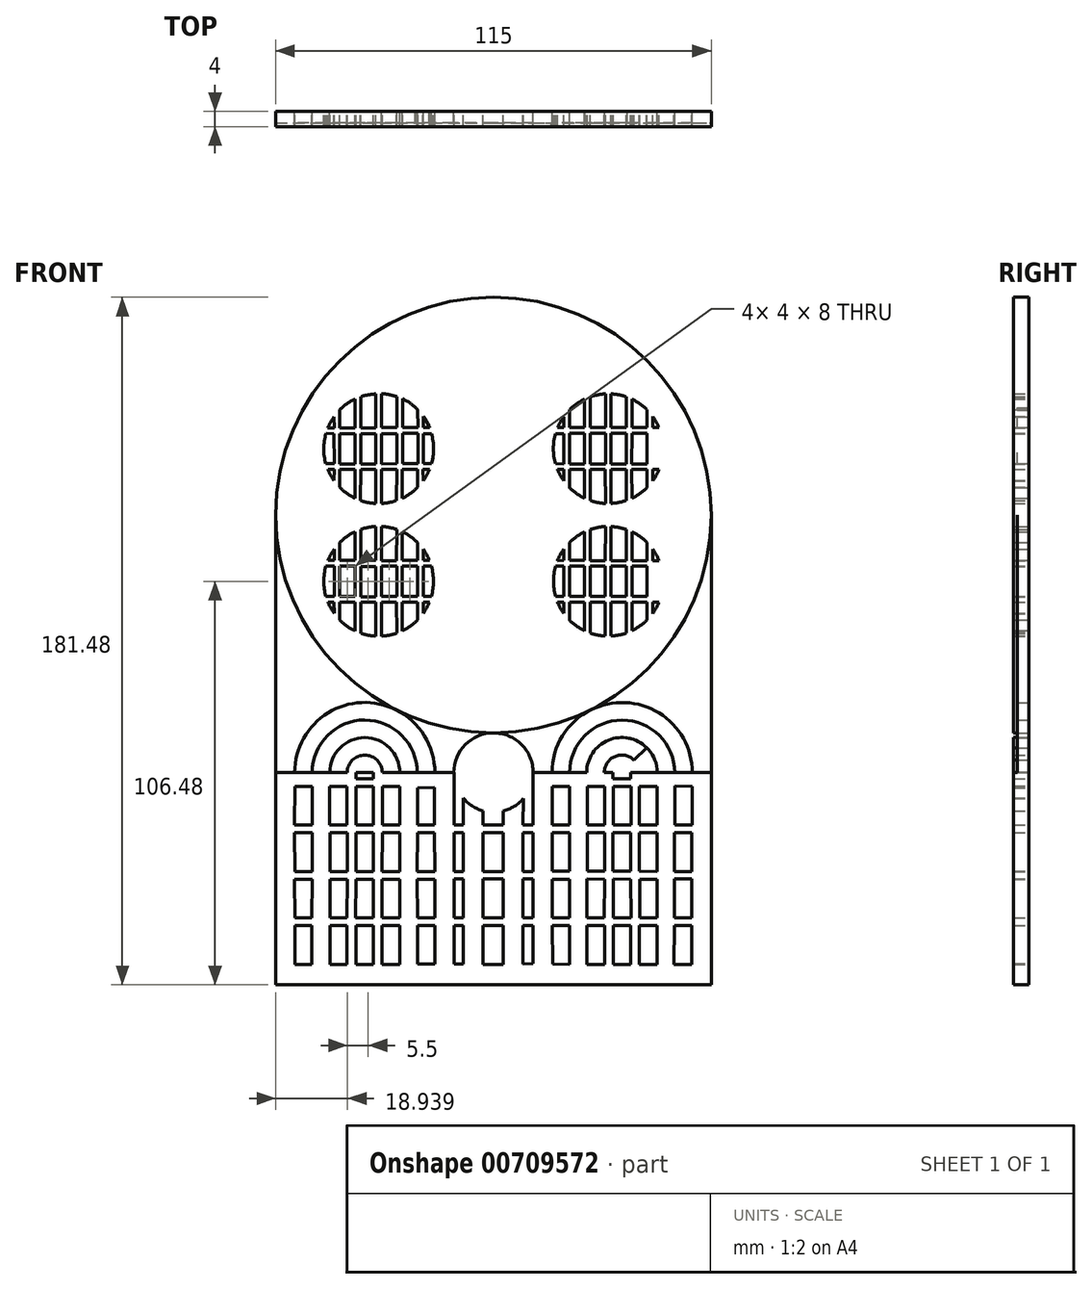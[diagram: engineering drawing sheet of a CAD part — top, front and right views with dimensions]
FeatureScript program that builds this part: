
annotation { "Feature Type Name" : "Feature", "Feature Type Description" : "" }
export const myFeature = defineFeature(function(context is Context, id is Id, definition is map)
    precondition{}
    {
        {
            var Q0;
            Q0=qCreatedBy(makeId("Front.planeOp"),FACE);
            var sketch = newSketch(context, id + "F0", { "sketchPlane" : qUnion([Q0])});
            skCircle(sketch, "E0", {"center": v(0, 0) * mm, "radius": 17.5 * mm});
            skPoint(sketch, "E1", {"position": v(0, 35) * mm});
            skPoint(sketch, "E2", {"position": v(-35, 0) * mm});
            skPoint(sketch, "E3", {"position": v(35, 0) * mm});
            skPoint(sketch, "E4", {"position": v(0, -35) * mm});
            skCircle(sketch, "E5", {"center": v(0, 0) * mm, "radius": 35 * mm});
            skPoint(sketch, "E6", {"position": v(-30.31, 17.5) * mm});
            skPoint(sketch, "E7", {"position": v(30.31, 17.5) * mm});
            skPoint(sketch, "E8", {"position": v(30.31, -17.5) * mm});
            skPoint(sketch, "E9", {"position": v(-30.31, -17.5) * mm});
            skCircle(sketch, "E10", {"center": v(-30.31, 17.5) * mm, "radius": 17.5 * mm});
            skCircle(sketch, "E11", {"center": v(30.31, 17.5) * mm, "radius": 17.5 * mm});
            skPoint(sketch, "E12", {"position": v(15.16, 8.75) * mm});
            skPoint(sketch, "E13", {"position": v(-15.16, -8.75) * mm});
            skCircle(sketch, "E14", {"center": v(-30.31, -17.5) * mm, "radius": 17.5 * mm});
            skCircle(sketch, "E15", {"center": v(0, -35) * mm, "radius": 17.5 * mm});
            skCircle(sketch, "E16", {"center": v(30.31, -17.5) * mm, "radius": 17.5 * mm});
            skCircle(sketch, "E17", {"center": v(0, 35) * mm, "radius": 17.5 * mm});
            skPoint(sketch, "E18", {"position": v(0, -52.5) * mm});
            skCircle(sketch, "E19", {"center": v(0, 0) * mm, "radius": 14.5 * mm});
            skCircle(sketch, "E20", {"center": v(-30.31, 17.5) * mm, "radius": 14.5 * mm});
            skCircle(sketch, "E21", {"center": v(0, 35) * mm, "radius": 14.5 * mm});
            skCircle(sketch, "E22", {"center": v(30.31, 17.5) * mm, "radius": 14.5 * mm});
            skCircle(sketch, "E23", {"center": v(30.31, -17.5) * mm, "radius": 14.5 * mm});
            skCircle(sketch, "E24", {"center": v(0, -35) * mm, "radius": 14.5 * mm});
            skCircle(sketch, "E25", {"center": v(-30.31, -17.5) * mm, "radius": 14.5 * mm});
            skArc(sketch, "E26", {"start": v(57.5, 0) * mm, "mid": v(0, 57.5) * mm, "end": v(-57.5, 0) * mm});
            skPoint(sketch, "E27", {"position": v(-20.96, 36.3) * mm});
            skArc(sketch, "E28", {"start": v(-20.96, 36.3) * mm, "mid": v(-28.74, 38.44) * mm, "end": v(-36.76, 37.49) * mm});
            skArc(sketch, "E29", {"start": v(-20.96, 36.3) * mm, "mid": v(-18.92, 44.11) * mm, "end": v(-14.09, 50.57) * mm});
            skPoint(sketch, "E30", {"position": v(14.09, 50.58) * mm});
            skPoint(sketch, "E31", {"position": v(41.92, 0) * mm});
            skArc(sketch, "E32", {"start": v(50.84, 13.09) * mm, "mid": v(47.66, 5.67) * mm, "end": v(41.92, 0) * mm});
            skArc(sketch, "E33", {"start": v(41.92, 0) * mm, "mid": v(47.66, -5.67) * mm, "end": v(50.84, -13.09) * mm});
            skPoint(sketch, "E34", {"position": v(20.96, 36.3) * mm});
            skArc(sketch, "E35", {"start": v(20.96, 36.3) * mm, "mid": v(28.74, 38.44) * mm, "end": v(36.76, 37.49) * mm});
            skArc(sketch, "E36", {"start": v(14.09, 50.58) * mm, "mid": v(18.92, 44.11) * mm, "end": v(20.96, 36.3) * mm});
            skArc(sketch, "E37", {"start": v(-50.84, -13.09) * mm, "mid": v(-47.66, -5.67) * mm, "end": v(-41.92, 0) * mm});
            skArc(sketch, "E38", {"start": v(-50.84, 13.09) * mm, "mid": v(-47.66, 5.67) * mm, "end": v(-41.92, 0) * mm});
            skArc(sketch, "E39", {"start": v(-50.84, -13.09) * mm, "mid": v(-52.5, 0) * mm, "end": v(-50.84, 13.09) * mm});
            skArc(sketch, "E40", {"start": v(-36.76, -37.49) * mm, "mid": v(-28.74, -38.44) * mm, "end": v(-20.96, -36.3) * mm});
            skArc(sketch, "E41", {"start": v(-20.96, -36.3) * mm, "mid": v(-18.92, -44.11) * mm, "end": v(-14.09, -50.58) * mm});
            skArc(sketch, "E42", {"start": v(-36.76, -37.49) * mm, "mid": v(-26.25, -45.47) * mm, "end": v(-14.09, -50.58) * mm});
            skArc(sketch, "E43", {"start": v(14.09, -50.58) * mm, "mid": v(18.92, -44.11) * mm, "end": v(20.96, -36.3) * mm});
            skArc(sketch, "E44", {"start": v(20.96, -36.3) * mm, "mid": v(28.74, -38.44) * mm, "end": v(36.76, -37.49) * mm});
            skArc(sketch, "E45", {"start": v(14.09, -50.58) * mm, "mid": v(26.25, -45.47) * mm, "end": v(36.76, -37.49) * mm});
            skArc(sketch, "E46", {"start": v(50.84, -13.09) * mm, "mid": v(52.5, 0) * mm, "end": v(50.84, 13.09) * mm, "construction": true});
            skArc(sketch, "E47", {"start": v(14.09, 50.58) * mm, "mid": v(26.25, 45.47) * mm, "end": v(36.76, 37.49) * mm});
            skArc(sketch, "E48", {"start": v(-36.76, 37.49) * mm, "mid": v(-26.25, 45.47) * mm, "end": v(-14.09, 50.58) * mm});
            skLineSegment(sketch, "E49", {"start": v(0, 0) * mm, "end": v(47.13, 81.64) * mm, "construction": true});
            skArc(sketch, "E50", {"start": v(50.84, 13.09) * mm, "mid": v(52.5, 0) * mm, "end": v(50.84, -13.09) * mm});
            skSolve(sketch);
        }
        {
            var Q0;
            Q0=qCreatedBy(makeId("Front.planeOp"),FACE);
            var sketch = newSketch(context, id + "F1", { "sketchPlane" : qUnion([Q0])});
            skArc(sketch, "E51", {"start": v(57.5, 0) * mm, "mid": v(0, 57.5) * mm, "end": v(-57.5, 0) * mm});
            skLineSegment(sketch, "E52", {"start": v(57.5, -67.99) * mm, "end": v(57.5, 0) * mm});
            skLineSegment(sketch, "E53", {"start": v(-57.5, 0) * mm, "end": v(-57.5, -67.99) * mm});
            skPoint(sketch, "E54", {"position": v(-52.5, -67.99) * mm});
            skLineSegment(sketch, "E55", {"start": v(-52.5, -67.99) * mm, "end": v(52.5, -67.99) * mm});
            skPoint(sketch, "E56", {"position": v(-52.5, -23.45) * mm});
            skLineSegment(sketch, "E57", {"start": v(-52.5, -23.45) * mm, "end": v(-52.5, -67.99) * mm});
            skLineSegment(sketch, "E58", {"start": v(52.5, -23.45) * mm, "end": v(52.5, -67.99) * mm});
            skArc(sketch, "E59", {"start": v(-52.5, -23.45) * mm, "mid": v(-31.29, -48.24) * mm, "end": v(0, -57.5) * mm});
            skArc(sketch, "E60", {"start": v(0, -57.5) * mm, "mid": v(31.29, -48.24) * mm, "end": v(52.5, -23.45) * mm});
            skArc(sketch, "E61", {"start": v(-15.48, -67.99) * mm, "mid": v(-33.99, -49.48) * mm, "end": v(-52.5, -67.99) * mm});
            skArc(sketch, "E62", {"start": v(52.5, -67.99) * mm, "mid": v(33.99, -49.48) * mm, "end": v(15.48, -67.99) * mm});
            skArc(sketch, "E63", {"start": v(-10.48, -67.99) * mm, "mid": v(0, -57.5) * mm, "end": v(10.48, -67.99) * mm});
            skLineSegment(sketch, "E64", {"start": v(-10.48, -67.99) * mm, "end": v(-10.48, -73.7) * mm, "construction": true});
            skLineSegment(sketch, "E65", {"start": v(10.48, -67.99) * mm, "end": v(10.48, -74.15) * mm, "construction": true});
            skLineSegment(sketch, "E66", {"start": v(15.48, -67.99) * mm, "end": v(15.48, -73.84) * mm, "construction": true});
            skLineSegment(sketch, "E67", {"start": v(52.5, -67.99) * mm, "end": v(52.5, -74.35) * mm, "construction": true});
            skLineSegment(sketch, "E68", {"start": v(-15.48, -67.99) * mm, "end": v(-15.48, -74.15) * mm, "construction": true});
            skLineSegment(sketch, "E69", {"start": v(-52.5, -67.99) * mm, "end": v(-52.5, -75.2) * mm, "construction": true});
            skLineSegment(sketch, "E70", {"start": v(-15.48, -72) * mm, "end": v(-10.48, -72) * mm, "construction": true});
            skLineSegment(sketch, "E71", {"start": v(10.48, -71.6) * mm, "end": v(15.49, -71.6) * mm, "construction": true});
            skLineSegment(sketch, "E72", {"start": v(52.5, -67.99) * mm, "end": v(57.5, -67.99) * mm, "construction": true});
            skLineSegment(sketch, "E73", {"start": v(-52.5, -67.99) * mm, "end": v(-57.5, -67.99) * mm, "construction": true});
            skCircle(sketch, "E74", {"center": v(0, 0) * mm, "radius": 57.5 * mm});
            skLineSegment(sketch, "E75", {"start": v(15.49, -71.6) * mm, "end": v(20.11, -71.6) * mm, "construction": true});
            skLineSegment(sketch, "E76", {"start": v(20.11, -71.6) * mm, "end": v(24.74, -71.6) * mm, "construction": true});
            skLineSegment(sketch, "E77", {"start": v(24.74, -71.6) * mm, "end": v(29.36, -71.6) * mm, "construction": true});
            skLineSegment(sketch, "E78", {"start": v(29.36, -71.6) * mm, "end": v(33.99, -71.6) * mm, "construction": true});
            skLineSegment(sketch, "E79", {"start": v(33.99, -71.6) * mm, "end": v(38.62, -71.6) * mm, "construction": true});
            skLineSegment(sketch, "E80", {"start": v(38.62, -71.6) * mm, "end": v(43.24, -71.6) * mm, "construction": true});
            skLineSegment(sketch, "E81", {"start": v(43.24, -71.6) * mm, "end": v(47.87, -71.6) * mm, "construction": true});
            skLineSegment(sketch, "E82", {"start": v(47.87, -71.6) * mm, "end": v(52.5, -71.6) * mm, "construction": true});
            skLineSegment(sketch, "E83", {"start": v(20.11, -71.6) * mm, "end": v(20.11, -67.99) * mm, "construction": true});
            skLineSegment(sketch, "E84", {"start": v(24.74, -71.6) * mm, "end": v(24.74, -67.99) * mm, "construction": true});
            skLineSegment(sketch, "E85", {"start": v(29.36, -71.6) * mm, "end": v(29.36, -67.99) * mm, "construction": true});
            skLineSegment(sketch, "E86", {"start": v(33.99, -71.6) * mm, "end": v(33.99, -67.99) * mm, "construction": true});
            skLineSegment(sketch, "E87", {"start": v(38.62, -71.6) * mm, "end": v(38.62, -67.99) * mm, "construction": true});
            skLineSegment(sketch, "E88", {"start": v(43.24, -71.6) * mm, "end": v(43.24, -67.99) * mm, "construction": true});
            skLineSegment(sketch, "E89", {"start": v(47.87, -71.6) * mm, "end": v(47.87, -67.99) * mm, "construction": true});
            skArc(sketch, "E90", {"start": v(47.87, -67.99) * mm, "mid": v(33.99, -54.1) * mm, "end": v(20.11, -67.99) * mm});
            skArc(sketch, "E91", {"start": v(43.24, -67.99) * mm, "mid": v(33.99, -58.74) * mm, "end": v(24.74, -67.99) * mm});
            skArc(sketch, "E92", {"start": v(38.62, -67.99) * mm, "mid": v(33.99, -63.36) * mm, "end": v(29.36, -67.99) * mm});
            skLineSegment(sketch, "E93", {"start": v(-15.48, -72) * mm, "end": v(-20.11, -72) * mm, "construction": true});
            skLineSegment(sketch, "E94", {"start": v(-20.11, -72) * mm, "end": v(-24.74, -72) * mm, "construction": true});
            skLineSegment(sketch, "E95", {"start": v(-24.74, -72) * mm, "end": v(-29.36, -72) * mm, "construction": true});
            skLineSegment(sketch, "E96", {"start": v(-29.36, -72) * mm, "end": v(-33.99, -72) * mm, "construction": true});
            skLineSegment(sketch, "E97", {"start": v(-33.99, -72) * mm, "end": v(-38.62, -72) * mm, "construction": true});
            skLineSegment(sketch, "E98", {"start": v(-38.62, -72) * mm, "end": v(-43.24, -72) * mm, "construction": true});
            skLineSegment(sketch, "E99", {"start": v(-43.24, -72) * mm, "end": v(-47.87, -72) * mm, "construction": true});
            skLineSegment(sketch, "E100", {"start": v(-47.87, -72) * mm, "end": v(-52.5, -72) * mm, "construction": true});
            skLineSegment(sketch, "E101", {"start": v(-47.87, -72) * mm, "end": v(-47.87, -67.99) * mm, "construction": true});
            skLineSegment(sketch, "E102", {"start": v(-43.24, -72) * mm, "end": v(-43.24, -67.99) * mm, "construction": true});
            skLineSegment(sketch, "E103", {"start": v(-38.62, -72) * mm, "end": v(-38.62, -67.99) * mm, "construction": true});
            skLineSegment(sketch, "E104", {"start": v(-29.36, -72) * mm, "end": v(-29.36, -67.99) * mm, "construction": true});
            skLineSegment(sketch, "E105", {"start": v(-24.74, -72) * mm, "end": v(-24.74, -67.99) * mm, "construction": true});
            skLineSegment(sketch, "E106", {"start": v(-20.11, -72) * mm, "end": v(-20.11, -67.99) * mm, "construction": true});
            skLineSegment(sketch, "E107", {"start": v(-33.99, -72) * mm, "end": v(-33.99, -67.99) * mm, "construction": true});
            skArc(sketch, "E108", {"start": v(-20.11, -67.99) * mm, "mid": v(-33.99, -54.1) * mm, "end": v(-47.87, -67.99) * mm});
            skArc(sketch, "E109", {"start": v(-24.74, -67.99) * mm, "mid": v(-33.99, -58.74) * mm, "end": v(-43.24, -67.99) * mm});
            skArc(sketch, "E110", {"start": v(-29.36, -67.99) * mm, "mid": v(-33.99, -63.36) * mm, "end": v(-38.62, -67.99) * mm});
            skLineSegment(sketch, "E111", {"start": v(-10.48, -72) * mm, "end": v(-7.86, -72) * mm, "construction": true});
            skLineSegment(sketch, "E112", {"start": v(-7.86, -72) * mm, "end": v(-5.24, -72) * mm, "construction": true});
            skLineSegment(sketch, "E113", {"start": v(-5.24, -72) * mm, "end": v(-2.62, -72) * mm, "construction": true});
            skLineSegment(sketch, "E114", {"start": v(-2.62, -72) * mm, "end": v(0, -72) * mm, "construction": true});
            skLineSegment(sketch, "E115", {"start": v(0, -72) * mm, "end": v(2.62, -72) * mm, "construction": true});
            skLineSegment(sketch, "E116", {"start": v(2.62, -72) * mm, "end": v(5.24, -72) * mm, "construction": true});
            skLineSegment(sketch, "E117", {"start": v(5.24, -72) * mm, "end": v(7.86, -72) * mm, "construction": true});
            skLineSegment(sketch, "E118", {"start": v(7.86, -72) * mm, "end": v(10.48, -72) * mm, "construction": true});
            skLineSegment(sketch, "E119", {"start": v(-7.86, -72) * mm, "end": v(-7.86, -67.99) * mm, "construction": true});
            skLineSegment(sketch, "E120", {"start": v(-5.24, -72) * mm, "end": v(-5.24, -67.99) * mm, "construction": true});
            skLineSegment(sketch, "E121", {"start": v(-2.62, -72) * mm, "end": v(-2.62, -67.99) * mm, "construction": true});
            skLineSegment(sketch, "E122", {"start": v(2.62, -72) * mm, "end": v(2.62, -67.99) * mm, "construction": true});
            skLineSegment(sketch, "E123", {"start": v(0, -72) * mm, "end": v(0, -67.98) * mm, "construction": true});
            skLineSegment(sketch, "E124", {"start": v(5.24, -72) * mm, "end": v(5.24, -67.99) * mm, "construction": true});
            skLineSegment(sketch, "E125", {"start": v(7.86, -72) * mm, "end": v(7.86, -67.99) * mm, "construction": true});
            skArc(sketch, "E126", {"start": v(7.86, -67.99) * mm, "mid": v(0, -60.13) * mm, "end": v(-7.86, -67.99) * mm});
            skArc(sketch, "E127", {"start": v(5.24, -67.99) * mm, "mid": v(0, -62.75) * mm, "end": v(-5.24, -67.99) * mm});
            skArc(sketch, "E128", {"start": v(2.62, -67.99) * mm, "mid": v(0, -65.37) * mm, "end": v(-2.62, -67.99) * mm});
            skLineSegment(sketch, "E129", {"start": v(-33.99, -67.99) * mm, "end": v(-33.99, -49.48) * mm, "construction": true});
            skLineSegment(sketch, "E130", {"start": v(33.99, -67.99) * mm, "end": v(33.99, -49.48) * mm, "construction": true});
            skLineSegment(sketch, "E131", {"start": v(0, -57.5) * mm, "end": v(0, -67.98) * mm, "construction": true});
            skLineSegment(sketch, "E132", {"start": v(-33.99, -67.99) * mm, "end": v(-47.08, -54.9) * mm, "construction": true});
            skLineSegment(sketch, "E133", {"start": v(-33.99, -67.99) * mm, "end": v(-20.9, -54.9) * mm, "construction": true});
            skLineSegment(sketch, "E134", {"start": v(33.99, -67.99) * mm, "end": v(20.9, -54.9) * mm, "construction": true});
            skLineSegment(sketch, "E135", {"start": v(33.99, -67.99) * mm, "end": v(47.08, -54.9) * mm, "construction": true});
            skLineSegment(sketch, "E136", {"start": v(0, -67.98) * mm, "end": v(7.41, -60.57) * mm, "construction": true});
            skLineSegment(sketch, "E137", {"start": v(0, -67.98) * mm, "end": v(-7.41, -60.57) * mm, "construction": true});
            skLineSegment(sketch, "E138", {"start": v(-57.5, -67.99) * mm, "end": v(-52.5, -67.99) * mm});
            skLineSegment(sketch, "E139", {"start": v(52.5, -67.99) * mm, "end": v(57.5, -67.99) * mm});
            skPoint(sketch, "E140", {"position": v(-29.56, -3.02) * mm});
            skPoint(sketch, "E141", {"position": v(-42.06, -21.5) * mm});
            skLineSegment(sketch, "E142.bottom", {"start": v(-40.56, -13.5) * mm, "end": v(-40.56, -13.5) * mm});
            skLineSegment(sketch, "E142.top", {"start": v(-40.56, -21.5) * mm, "end": v(-40.56, -21.5) * mm});
            skLineSegment(sketch, "E142.left", {"start": v(-40.56, -13.5) * mm, "end": v(-40.56, -21.5) * mm});
            skLineSegment(sketch, "E142.right", {"start": v(-40.56, -13.5) * mm, "end": v(-40.56, -21.5) * mm});
            skLineSegment(sketch, "E143.bottom", {"start": v(-36.56, -21.5) * mm, "end": v(-36.57, -21.5) * mm});
            skLineSegment(sketch, "E143.top", {"start": v(-36.56, -13.5) * mm, "end": v(-36.57, -13.5) * mm});
            skLineSegment(sketch, "E143.left", {"start": v(-36.57, -21.5) * mm, "end": v(-36.57, -13.5) * mm});
            skLineSegment(sketch, "E143.right", {"start": v(-36.56, -21.5) * mm, "end": v(-36.56, -13.5) * mm});
            skLineSegment(sketch, "E144.bottom", {"start": v(-35.06, -13.56) * mm, "end": v(-31.06, -13.56) * mm});
            skLineSegment(sketch, "E144.top", {"start": v(-35.06, -21.56) * mm, "end": v(-31.06, -21.56) * mm});
            skLineSegment(sketch, "E144.left", {"start": v(-35.06, -13.56) * mm, "end": v(-35.06, -21.56) * mm});
            skLineSegment(sketch, "E144.right", {"start": v(-31.06, -13.56) * mm, "end": v(-31.06, -21.56) * mm});
            skLineSegment(sketch, "E145.bottom", {"start": v(-29.56, -13.52) * mm, "end": v(-25.56, -13.52) * mm});
            skLineSegment(sketch, "E145.top", {"start": v(-29.56, -21.52) * mm, "end": v(-25.56, -21.52) * mm});
            skLineSegment(sketch, "E145.left", {"start": v(-29.56, -13.52) * mm, "end": v(-29.56, -21.52) * mm});
            skLineSegment(sketch, "E145.right", {"start": v(-25.56, -13.52) * mm, "end": v(-25.56, -21.52) * mm});
            skLineSegment(sketch, "E146.bottom", {"start": v(-24.06, -13.5) * mm, "end": v(-20.06, -13.5) * mm});
            skLineSegment(sketch, "E146.top", {"start": v(-24.06, -21.5) * mm, "end": v(-20.06, -21.5) * mm});
            skLineSegment(sketch, "E146.left", {"start": v(-24.06, -13.5) * mm, "end": v(-24.06, -21.5) * mm});
            skLineSegment(sketch, "E146.right", {"start": v(-20.06, -13.5) * mm, "end": v(-20.06, -21.5) * mm});
            skLineSegment(sketch, "E147.bottom", {"start": v(-40.56, -13.5) * mm, "end": v(-36.57, -13.5) * mm});
            skLineSegment(sketch, "E147.top", {"start": v(-40.56, -21.5) * mm, "end": v(-36.57, -21.5) * mm});
            skLineSegment(sketch, "E147.right", {"start": v(-36.57, -13.5) * mm, "end": v(-36.57, -21.5) * mm});
            skLineSegment(sketch, "E148.bottom", {"start": v(-35.06, -23) * mm, "end": v(-31.06, -23) * mm});
            skLineSegment(sketch, "E149.bottom", {"start": v(-29.56, -23) * mm, "end": v(-25.57, -23) * mm});
            skLineSegment(sketch, "E150", {"start": v(-40.56, -13.5) * mm, "end": v(-36.56, -13.5) * mm});
            skLineSegment(sketch, "E151", {"start": v(-40.56, -12) * mm, "end": v(-36.56, -12) * mm});
            skLineSegment(sketch, "E152", {"start": v(-29.56, -12.02) * mm, "end": v(-25.56, -12.02) * mm});
            skLineSegment(sketch, "E153", {"start": v(-24.06, -12) * mm, "end": v(-20.06, -12) * mm});
            skLineSegment(sketch, "E154", {"start": v(-35.3, -3.87) * mm, "end": v(-35.3, -3.86) * mm});
            skLineSegment(sketch, "E155", {"start": v(-40.56, -23) * mm, "end": v(-36.56, -23) * mm});
            skLineSegment(sketch, "E156", {"start": v(-44.24, -13.5) * mm, "end": v(-42.06, -13.5) * mm});
            skLineSegment(sketch, "E157", {"start": v(-42.06, -13.5) * mm, "end": v(-42.06, -21.5) * mm});
            skLineSegment(sketch, "E158", {"start": v(-18.56, -21.5) * mm, "end": v(-16.38, -21.5) * mm});
            skLineSegment(sketch, "E159", {"start": v(-18.56, -13.52) * mm, "end": v(-18.56, -21.5) * mm});
            skPoint(sketch, "E160", {"position": v(0, -124.5) * mm});
            skLineSegment(sketch, "E161", {"start": v(57.5, -124.17) * mm, "end": v(-57.5, -124.17) * mm});
            skArc(sketch, "E162", {"start": v(-44.24, -13.5) * mm, "mid": v(-44.8, -17.5) * mm, "end": v(-44.24, -21.51) * mm});
            skArc(sketch, "E163", {"start": v(-16.4, -13.5) * mm, "mid": v(-15.83, -17.5) * mm, "end": v(-16.39, -21.5) * mm});
            skPoint(sketch, "E164", {"position": v(-44.24, -21.5) * mm});
            skLineSegment(sketch, "E165", {"start": v(-44.24, -21.5) * mm, "end": v(-42.06, -21.5) * mm});
            skPoint(sketch, "E166", {"position": v(-36.56, -12) * mm});
            skLineSegment(sketch, "E167", {"start": v(-35.06, -12) * mm, "end": v(-31.06, -12) * mm});
            skPoint(sketch, "E168", {"position": v(-35.07, -3.8) * mm});
            skPoint(sketch, "E169", {"position": v(-31.07, -3.02) * mm});
            skArc(sketch, "E170", {"start": v(-35.07, -3.8) * mm, "mid": v(-33.1, -3.28) * mm, "end": v(-31.07, -3.03) * mm});
            skArc(sketch, "E171", {"start": v(-29.56, -3.02) * mm, "mid": v(-27.53, -3.27) * mm, "end": v(-25.56, -3.8) * mm});
            skPoint(sketch, "E172", {"position": v(-36.57, -4.42) * mm});
            skPoint(sketch, "E173", {"position": v(-24.06, -4.41) * mm});
            skLineSegment(sketch, "E174", {"start": v(-20.07, -7.24) * mm, "end": v(-20.06, -12) * mm});
            skPoint(sketch, "E175", {"position": v(-18.57, -12) * mm});
            skPoint(sketch, "E176", {"position": v(-18.56, -9.01) * mm});
            skPoint(sketch, "E177", {"position": v(-16.92, -12) * mm});
            skLineSegment(sketch, "E178", {"start": v(-18.56, -9.01) * mm, "end": v(-18.57, -12) * mm});
            skPoint(sketch, "E179", {"position": v(-42.06, -9) * mm});
            skPoint(sketch, "E180", {"position": v(-42.06, -12) * mm});
            skPoint(sketch, "E181", {"position": v(-43.72, -12) * mm});
            skLineSegment(sketch, "E182", {"start": v(-43.72, -12) * mm, "end": v(-42.06, -12) * mm});
            skLineSegment(sketch, "E183", {"start": v(-42.06, -12) * mm, "end": v(-42.06, -9) * mm});
            skArc(sketch, "E184", {"start": v(-43.72, -12) * mm, "mid": v(-42.98, -10.47) * mm, "end": v(-42.06, -9.03) * mm});
            skArc(sketch, "E185", {"start": v(-18.56, -9.01) * mm, "mid": v(-17.64, -10.46) * mm, "end": v(-16.9, -12) * mm});
            skPoint(sketch, "E186", {"position": v(-42.06, -25.98) * mm});
            skPoint(sketch, "E187", {"position": v(-42.09, -23) * mm});
            skPoint(sketch, "E188", {"position": v(-43.7, -23) * mm});
            skLineSegment(sketch, "E189", {"start": v(-43.7, -23) * mm, "end": v(-42.09, -23) * mm});
            skLineSegment(sketch, "E190", {"start": v(-42.09, -23) * mm, "end": v(-42.06, -25.98) * mm});
            skArc(sketch, "E191", {"start": v(-43.7, -23) * mm, "mid": v(-42.97, -24.52) * mm, "end": v(-42.06, -25.94) * mm});
            skPoint(sketch, "E192", {"position": v(-31.07, -31.97) * mm});
            skPoint(sketch, "E193", {"position": v(-25.56, -31.19) * mm});
            skPoint(sketch, "E194", {"position": v(-20.06, -27.74) * mm});
            skLineSegment(sketch, "E195", {"start": v(-24.06, -23) * mm, "end": v(-20.06, -23) * mm});
            skPoint(sketch, "E196", {"position": v(-18.56, -22.98) * mm});
            skPoint(sketch, "E197", {"position": v(-16.92, -22.98) * mm});
            skPoint(sketch, "E198", {"position": v(-18.56, -25.95) * mm});
            skLineSegment(sketch, "E199", {"start": v(-18.56, -25.95) * mm, "end": v(-18.56, -22.98) * mm});
            skArc(sketch, "E200", {"start": v(-16.92, -22.98) * mm, "mid": v(-17.65, -24.51) * mm, "end": v(-18.56, -25.95) * mm});
            skLineSegment(sketch, "E201", {"start": v(-18.56, -22.98) * mm, "end": v(-16.92, -22.98) * mm});
            skPoint(sketch, "E202", {"position": v(-35.06, -31.2) * mm});
            skLineSegment(sketch, "E203", {"start": v(-18.57, -12) * mm, "end": v(-16.9, -12) * mm});
            skPoint(sketch, "E204", {"position": v(-24.06, -30.58) * mm});
            skArc(sketch, "E205", {"start": v(-31.07, -31.97) * mm, "mid": v(-33.1, -31.72) * mm, "end": v(-35.06, -31.2) * mm});
            skPoint(sketch, "E206", {"position": v(-29.56, -31.97) * mm});
            skArc(sketch, "E207", {"start": v(-25.56, -31.19) * mm, "mid": v(-27.53, -31.72) * mm, "end": v(-29.56, -31.97) * mm});
            skLineSegment(sketch, "E208", {"start": v(-35.07, -3.8) * mm, "end": v(-35.06, -12) * mm});
            skLineSegment(sketch, "E209", {"start": v(-31.07, -3.02) * mm, "end": v(-31.06, -12) * mm});
            skLineSegment(sketch, "E210", {"start": v(-29.56, -3.02) * mm, "end": v(-29.56, -12.02) * mm});
            skPoint(sketch, "E211", {"position": v(-25.56, -3.8) * mm});
            skLineSegment(sketch, "E212", {"start": v(-25.56, -3.8) * mm, "end": v(-25.56, -12.02) * mm});
            skPoint(sketch, "E213", {"position": v(-40.56, -7.25) * mm});
            skLineSegment(sketch, "E214", {"start": v(-36.57, -4.42) * mm, "end": v(-36.56, -12) * mm});
            skLineSegment(sketch, "E215", {"start": v(-40.56, -7.25) * mm, "end": v(-40.56, -12) * mm});
            skArc(sketch, "E216", {"start": v(-40.56, -7.25) * mm, "mid": v(-38.69, -5.66) * mm, "end": v(-36.57, -4.42) * mm});
            skArc(sketch, "E217", {"start": v(-24.06, -4.41) * mm, "mid": v(-21.94, -5.66) * mm, "end": v(-20.07, -7.25) * mm});
            skLineSegment(sketch, "E218", {"start": v(-24.06, -4.41) * mm, "end": v(-24.06, -12) * mm});
            skLineSegment(sketch, "E219", {"start": v(-20.07, -7.25) * mm, "end": v(-20.06, -12) * mm});
            skPoint(sketch, "E220", {"position": v(-40.56, -27.75) * mm});
            skPoint(sketch, "E221", {"position": v(-36.57, -30.57) * mm});
            skLineSegment(sketch, "E222", {"start": v(-40.56, -23) * mm, "end": v(-40.56, -27.75) * mm});
            skLineSegment(sketch, "E223", {"start": v(-36.56, -23) * mm, "end": v(-36.57, -30.57) * mm});
            skArc(sketch, "E224", {"start": v(-40.56, -27.75) * mm, "mid": v(-38.69, -29.33) * mm, "end": v(-36.57, -30.57) * mm});
            skLineSegment(sketch, "E225", {"start": v(-35.06, -23) * mm, "end": v(-35.06, -31.2) * mm});
            skLineSegment(sketch, "E226", {"start": v(-31.06, -23) * mm, "end": v(-31.07, -31.97) * mm});
            skLineSegment(sketch, "E227", {"start": v(-29.56, -23) * mm, "end": v(-29.56, -31.97) * mm});
            skLineSegment(sketch, "E228", {"start": v(-25.57, -23) * mm, "end": v(-25.56, -31.19) * mm});
            skLineSegment(sketch, "E229", {"start": v(-24.06, -23) * mm, "end": v(-24.06, -30.58) * mm});
            skLineSegment(sketch, "E230", {"start": v(-20.06, -23) * mm, "end": v(-20.06, -27.74) * mm});
            skArc(sketch, "E231", {"start": v(-20.06, -27.74) * mm, "mid": v(-21.94, -29.32) * mm, "end": v(-24.06, -30.57) * mm});
            skPoint(sketch, "E232", {"position": v(-42.1, 21.5) * mm});
            skPoint(sketch, "E233", {"position": v(-44.82, 17.5) * mm});
            skPoint(sketch, "E234", {"position": v(-42.08, 17.5) * mm});
            skPoint(sketch, "E235", {"position": v(-40.57, 17.5) * mm});
            skPoint(sketch, "E236", {"position": v(-42.07, 23) * mm});
            skPoint(sketch, "E237", {"position": v(-44.24, 21.53) * mm});
            skPoint(sketch, "E238", {"position": v(-43.74, 23) * mm});
            skLineSegment(sketch, "E239", {"start": v(-43.74, 23) * mm, "end": v(-42.07, 23) * mm});
            skLineSegment(sketch, "E240", {"start": v(-44.24, 21.53) * mm, "end": v(-42.1, 21.5) * mm});
            skLineSegment(sketch, "E241", {"start": v(-40.57, 23) * mm, "end": v(-36.56, 23) * mm});
            skLineSegment(sketch, "E242", {"start": v(-40.57, 21.5) * mm, "end": v(-36.56, 21.5) * mm});
            skLineSegment(sketch, "E243", {"start": v(-35.07, 23.04) * mm, "end": v(-31.04, 23.04) * mm});
            skLineSegment(sketch, "E244", {"start": v(-35.07, 21.5) * mm, "end": v(-31.04, 21.5) * mm});
            skLineSegment(sketch, "E245", {"start": v(-35.07, 31.2) * mm, "end": v(-35.07, 23.04) * mm});
            skLineSegment(sketch, "E246", {"start": v(-36.54, 30.6) * mm, "end": v(-36.56, 23) * mm});
            skPoint(sketch, "E247", {"position": v(-40.56, 27.8) * mm});
            skPoint(sketch, "E248", {"position": v(-42.08, 25.99) * mm});
            skLineSegment(sketch, "E249", {"start": v(-40.56, 27.8) * mm, "end": v(-40.57, 23) * mm});
            skLineSegment(sketch, "E250", {"start": v(-42.08, 25.99) * mm, "end": v(-42.07, 23) * mm});
            skPoint(sketch, "E251", {"position": v(-40.57, 13.5) * mm});
            skPoint(sketch, "E252", {"position": v(-36.58, 13.5) * mm});
            skPoint(sketch, "E253", {"position": v(-35.07, 13.5) * mm});
            skPoint(sketch, "E254", {"position": v(-31.08, 13.5) * mm});
            skPoint(sketch, "E255", {"position": v(-29.54, 13.5) * mm});
            skLineSegment(sketch, "E256", {"start": v(-40.57, 21.5) * mm, "end": v(-40.57, 13.5) * mm});
            skLineSegment(sketch, "E257", {"start": v(-36.56, 21.5) * mm, "end": v(-36.58, 13.5) * mm});
            skLineSegment(sketch, "E258", {"start": v(-35.07, 21.5) * mm, "end": v(-35.07, 13.5) * mm});
            skLineSegment(sketch, "E259", {"start": v(-31.04, 21.5) * mm, "end": v(-31.08, 13.5) * mm});
            skLineSegment(sketch, "E260", {"start": v(-40.57, 13.5) * mm, "end": v(-36.58, 13.5) * mm});
            skLineSegment(sketch, "E261", {"start": v(-35.07, 13.5) * mm, "end": v(-31.08, 13.5) * mm});
            skPoint(sketch, "E262", {"position": v(-44.27, 13.52) * mm});
            skPoint(sketch, "E263", {"position": v(-42.07, 13.52) * mm});
            skLineSegment(sketch, "E264", {"start": v(-44.27, 13.52) * mm, "end": v(-42.07, 13.52) * mm});
            skPoint(sketch, "E265", {"position": v(-29.6, 23.04) * mm});
            skPoint(sketch, "E266", {"position": v(-29.6, 21.5) * mm});
            skPoint(sketch, "E267", {"position": v(-25.47, 23.1) * mm});
            skPoint(sketch, "E268", {"position": v(-23.93, 23.1) * mm});
            skPoint(sketch, "E269", {"position": v(-19.94, 23.1) * mm});
            skPoint(sketch, "E270", {"position": v(-16.82, 23.1) * mm});
            skPoint(sketch, "E271", {"position": v(-18.46, 23.1) * mm});
            skPoint(sketch, "E272", {"position": v(-25.47, 21.5) * mm});
            skPoint(sketch, "E273", {"position": v(-23.93, 21.55) * mm});
            skPoint(sketch, "E274", {"position": v(-19.94, 21.55) * mm});
            skPoint(sketch, "E275", {"position": v(-18.57, 21.5) * mm});
            skPoint(sketch, "E276", {"position": v(-16.39, 21.5) * mm});
            skPoint(sketch, "E277", {"position": v(-25.47, 13.58) * mm});
            skPoint(sketch, "E278", {"position": v(-23.93, 13.58) * mm});
            skPoint(sketch, "E279", {"position": v(-19.94, 13.58) * mm});
            skPoint(sketch, "E280", {"position": v(-18.57, 13.52) * mm});
            skPoint(sketch, "E281", {"position": v(-16.35, 13.53) * mm});
            skLineSegment(sketch, "E282", {"start": v(-29.6, 23.04) * mm, "end": v(-25.47, 23.1) * mm});
            skLineSegment(sketch, "E283", {"start": v(-23.93, 23.1) * mm, "end": v(-19.94, 23.1) * mm});
            skLineSegment(sketch, "E284", {"start": v(-18.46, 23.1) * mm, "end": v(-16.82, 23.1) * mm});
            skLineSegment(sketch, "E285", {"start": v(-29.6, 21.5) * mm, "end": v(-25.47, 21.5) * mm});
            skLineSegment(sketch, "E286", {"start": v(-23.93, 21.55) * mm, "end": v(-19.94, 21.55) * mm});
            skLineSegment(sketch, "E287", {"start": v(-18.57, 21.5) * mm, "end": v(-16.39, 21.5) * mm});
            skLineSegment(sketch, "E288", {"start": v(-29.54, 13.5) * mm, "end": v(-25.47, 13.58) * mm});
            skLineSegment(sketch, "E289", {"start": v(-23.93, 13.58) * mm, "end": v(-19.94, 13.58) * mm});
            skLineSegment(sketch, "E290", {"start": v(-29.6, 21.5) * mm, "end": v(-29.54, 13.5) * mm});
            skLineSegment(sketch, "E291", {"start": v(-25.47, 21.5) * mm, "end": v(-25.47, 13.58) * mm});
            skLineSegment(sketch, "E292", {"start": v(-23.93, 21.55) * mm, "end": v(-23.93, 13.58) * mm});
            skLineSegment(sketch, "E293", {"start": v(-19.94, 21.55) * mm, "end": v(-19.94, 13.58) * mm});
            skLineSegment(sketch, "E294", {"start": v(-18.57, 21.5) * mm, "end": v(-18.57, 13.52) * mm});
            skPoint(sketch, "E295", {"position": v(-40.57, 12) * mm});
            skPoint(sketch, "E296", {"position": v(-36.59, 12.05) * mm});
            skPoint(sketch, "E297", {"position": v(-35.07, 12.05) * mm});
            skPoint(sketch, "E298", {"position": v(-31.08, 12.05) * mm});
            skPoint(sketch, "E299", {"position": v(-29.56, 12.05) * mm});
            skPoint(sketch, "E300", {"position": v(-25.55, 12.05) * mm});
            skPoint(sketch, "E301", {"position": v(-24.08, 12.05) * mm});
            skPoint(sketch, "E302", {"position": v(-20.06, 12.05) * mm});
            skPoint(sketch, "E303", {"position": v(-18.6, 12.05) * mm});
            skPoint(sketch, "E304", {"position": v(-16.9, 12.05) * mm});
            skPoint(sketch, "E305", {"position": v(-40.57, 7.3) * mm});
            skPoint(sketch, "E306", {"position": v(-36.6, 4.43) * mm});
            skPoint(sketch, "E307", {"position": v(-35.09, 3.8) * mm});
            skPoint(sketch, "E308", {"position": v(-31.1, 3.06) * mm});
            skPoint(sketch, "E309", {"position": v(-29.56, 3.05) * mm});
            skPoint(sketch, "E310", {"position": v(-25.6, 3.8) * mm});
            skPoint(sketch, "E311", {"position": v(-24.05, 4.43) * mm});
            skPoint(sketch, "E312", {"position": v(-20.07, 7.3) * mm});
            skPoint(sketch, "E313", {"position": v(-18.54, 9.06) * mm});
            skLineSegment(sketch, "E314", {"start": v(-40.57, 12) * mm, "end": v(-36.59, 12.05) * mm});
            skLineSegment(sketch, "E315", {"start": v(-35.07, 12.05) * mm, "end": v(-31.08, 12.05) * mm});
            skLineSegment(sketch, "E316", {"start": v(-29.56, 12.05) * mm, "end": v(-25.55, 12.05) * mm});
            skLineSegment(sketch, "E317", {"start": v(-24.08, 12.05) * mm, "end": v(-20.06, 12.05) * mm});
            skLineSegment(sketch, "E318", {"start": v(-18.6, 12.05) * mm, "end": v(-16.9, 12.05) * mm});
            skLineSegment(sketch, "E319", {"start": v(-40.57, 12) * mm, "end": v(-40.57, 7.3) * mm});
            skLineSegment(sketch, "E320", {"start": v(-36.59, 12.05) * mm, "end": v(-36.6, 4.43) * mm});
            skLineSegment(sketch, "E321", {"start": v(-35.07, 12.05) * mm, "end": v(-35.09, 3.8) * mm});
            skLineSegment(sketch, "E322", {"start": v(-31.08, 12.05) * mm, "end": v(-31.1, 3.06) * mm});
            skLineSegment(sketch, "E323", {"start": v(-29.56, 12.05) * mm, "end": v(-29.56, 3.05) * mm});
            skLineSegment(sketch, "E324", {"start": v(-25.55, 12.05) * mm, "end": v(-25.6, 3.8) * mm});
            skLineSegment(sketch, "E325", {"start": v(-24.08, 12.05) * mm, "end": v(-24.05, 4.43) * mm});
            skLineSegment(sketch, "E326", {"start": v(-20.06, 12.05) * mm, "end": v(-20.07, 7.3) * mm});
            skLineSegment(sketch, "E327", {"start": v(-18.6, 12.05) * mm, "end": v(-18.54, 9.06) * mm});
            skPoint(sketch, "E328", {"position": v(-29.58, 32.04) * mm});
            skPoint(sketch, "E329", {"position": v(-25.55, 31.25) * mm});
            skPoint(sketch, "E330", {"position": v(-23.98, 30.68) * mm});
            skPoint(sketch, "E331", {"position": v(-18.49, 26.07) * mm});
            skLineSegment(sketch, "E332", {"start": v(-29.58, 32.04) * mm, "end": v(-29.6, 23.04) * mm});
            skLineSegment(sketch, "E333", {"start": v(-23.98, 30.68) * mm, "end": v(-23.93, 23.1) * mm});
            skLineSegment(sketch, "E334", {"start": v(-18.49, 26.07) * mm, "end": v(-18.46, 23.1) * mm});
            skArc(sketch, "E335", {"start": v(-44.27, 13.52) * mm, "mid": v(-44.81, 17.53) * mm, "end": v(-44.22, 21.53) * mm});
            skArc(sketch, "E336", {"start": v(-43.74, 23) * mm, "mid": v(-43, 24.53) * mm, "end": v(-42.08, 25.96) * mm});
            skArc(sketch, "E337", {"start": v(-40.56, 27.8) * mm, "mid": v(-38.67, 29.37) * mm, "end": v(-36.54, 30.6) * mm});
            skArc(sketch, "E338", {"start": v(-35.07, 31.2) * mm, "mid": v(-33.1, 31.71) * mm, "end": v(-31.08, 31.95) * mm});
            skArc(sketch, "E339", {"start": v(-29.58, 32.04) * mm, "mid": v(-27.56, 31.79) * mm, "end": v(-25.6, 31.25) * mm});
            skArc(sketch, "E340", {"start": v(-23.98, 30.68) * mm, "mid": v(-21.88, 29.43) * mm, "end": v(-20.01, 27.86) * mm});
            skArc(sketch, "E341", {"start": v(-18.49, 26.07) * mm, "mid": v(-17.57, 24.63) * mm, "end": v(-16.82, 23.1) * mm});
            skArc(sketch, "E342", {"start": v(-16.39, 21.5) * mm, "mid": v(-15.81, 17.52) * mm, "end": v(-16.35, 13.53) * mm});
            skArc(sketch, "E343", {"start": v(-44.22, 21.53) * mm, "mid": v(-44.81, 17.53) * mm, "end": v(-44.27, 13.52) * mm});
            skArc(sketch, "E344", {"start": v(-40.57, 7.3) * mm, "mid": v(-38.7, 5.72) * mm, "end": v(-36.6, 4.48) * mm});
            skArc(sketch, "E345", {"start": v(-29.56, 3.05) * mm, "mid": v(-27.55, 3.3) * mm, "end": v(-25.6, 3.85) * mm});
            skArc(sketch, "E346", {"start": v(-24.05, 4.43) * mm, "mid": v(-21.94, 5.7) * mm, "end": v(-20.07, 7.3) * mm});
            skArc(sketch, "E347", {"start": v(-18.54, 9.06) * mm, "mid": v(-17.64, 10.5) * mm, "end": v(-16.9, 12.05) * mm});
            skLineSegment(sketch, "E348", {"start": v(-42.1, 21.5) * mm, "end": v(-42.07, 13.52) * mm});
            skLineSegment(sketch, "E349", {"start": v(-20.01, 27.86) * mm, "end": v(-19.94, 23.1) * mm});
            skLineSegment(sketch, "E350", {"start": v(-25.55, 31.25) * mm, "end": v(-25.47, 23.1) * mm});
            skLineSegment(sketch, "E351", {"start": v(-31.08, 31.95) * mm, "end": v(-31.04, 23.04) * mm});
            skArc(sketch, "E352", {"start": v(-29.58, 32.04) * mm, "mid": v(-27.53, 31.78) * mm, "end": v(-25.55, 31.24) * mm});
            skPoint(sketch, "E353", {"position": v(-18.56, -13.52) * mm});
            skLineSegment(sketch, "E354", {"start": v(-18.56, -13.52) * mm, "end": v(-16.4, -13.5) * mm});
            skArc(sketch, "E355", {"start": v(-31.1, 3.06) * mm, "mid": v(-33.12, 3.3) * mm, "end": v(-35.09, 3.82) * mm});
            skLineSegment(sketch, "E356", {"start": v(-18.57, 13.52) * mm, "end": v(-16.35, 13.53) * mm});
            skLineSegment(sketch, "E357", {"start": v(-16.35, 13.53) * mm, "end": v(-16.35, 13.53) * mm});
            skPoint(sketch, "E358", {"position": v(-42.06, 12) * mm});
            skPoint(sketch, "E359", {"position": v(-43.71, 12) * mm});
            skLineSegment(sketch, "E360", {"start": v(-43.71, 12) * mm, "end": v(-42.06, 12) * mm});
            skPoint(sketch, "E361", {"position": v(-30.31, 17.5) * mm});
            skArc(sketch, "E362", {"start": v(-43.71, 12) * mm, "mid": v(-43.01, 10.53) * mm, "end": v(-42.15, 9.15) * mm});
            skLineSegment(sketch, "E363", {"start": v(-42.06, 12) * mm, "end": v(-42.15, 9.15) * mm});
            skPoint(sketch, "E364", {"position": v(30.2, 0) * mm});
            skPoint(sketch, "E365", {"position": v(26.32, 0) * mm});
            skPoint(sketch, "E366", {"position": v(33.98, 0) * mm});
            skPoint(sketch, "E367", {"position": v(30.3, -19.07) * mm});
            skLineSegment(sketch, "E368", {"start": v(30.3, -19.07) * mm, "end": v(30.3, 36.91) * mm});
            skLineSegment(sketch, "E369", {"start": v(30.3, -19.07) * mm, "end": v(30.32, -28.27) * mm});
            skPoint(sketch, "E370", {"position": v(30.3, 21.53) * mm});
            skPoint(sketch, "E371", {"position": v(30.27, 13.53) * mm});
            skPoint(sketch, "E372", {"position": v(30.27, 12.02) * mm});
            skPoint(sketch, "E373", {"position": v(30.3, 23.05) * mm});
            skPoint(sketch, "E374", {"position": v(31.06, 23.05) * mm});
            skPoint(sketch, "E375", {"position": v(35.06, 23.06) * mm});
            skPoint(sketch, "E376", {"position": v(25.56, 23.06) * mm});
            skPoint(sketch, "E377", {"position": v(30.3, 32.01) * mm});
            skPoint(sketch, "E378", {"position": v(24.06, 23.06) * mm});
            skPoint(sketch, "E379", {"position": v(35.07, 31.2) * mm});
            skPoint(sketch, "E380", {"position": v(36.56, 23.06) * mm});
            skPoint(sketch, "E381", {"position": v(29.56, 23.05) * mm});
            skPoint(sketch, "E382", {"position": v(20.06, 23.06) * mm});
            skPoint(sketch, "E383", {"position": v(18.56, 23.06) * mm});
            skPoint(sketch, "E384", {"position": v(40.56, 23.05) * mm});
            skPoint(sketch, "E385", {"position": v(42.06, 23.06) * mm});
            skPoint(sketch, "E386", {"position": v(16.35, -21.45) * mm});
            skPoint(sketch, "E387", {"position": v(16.9, -22.98) * mm});
            skPoint(sketch, "E388", {"position": v(18.56, -25.97) * mm});
            skPoint(sketch, "E389", {"position": v(18.56, -22.98) * mm});
            skPoint(sketch, "E390", {"position": v(20.06, -22.98) * mm});
            skPoint(sketch, "E391", {"position": v(24.05, -22.98) * mm});
            skPoint(sketch, "E392", {"position": v(25.56, -22.98) * mm});
            skPoint(sketch, "E393", {"position": v(20.06, -27.74) * mm});
            skPoint(sketch, "E394", {"position": v(24.05, -30.56) * mm});
            skPoint(sketch, "E395", {"position": v(25.56, -31.17) * mm});
            skPoint(sketch, "E396", {"position": v(29.54, -31.95) * mm});
            skPoint(sketch, "E397", {"position": v(31.05, -31.95) * mm});
            skPoint(sketch, "E398", {"position": v(35.05, -31.17) * mm});
            skPoint(sketch, "E399", {"position": v(36.56, -30.56) * mm});
            skPoint(sketch, "E400", {"position": v(24.05, -21.49) * mm});
            skPoint(sketch, "E401", {"position": v(25.56, -21.49) * mm});
            skPoint(sketch, "E402", {"position": v(30.31, -21.49) * mm});
            skPoint(sketch, "E403", {"position": v(30.32, -22.98) * mm});
            skPoint(sketch, "E404", {"position": v(31.05, -21.49) * mm});
            skPoint(sketch, "E405", {"position": v(31.05, -22.98) * mm});
            skPoint(sketch, "E406", {"position": v(29.54, -21.49) * mm});
            skPoint(sketch, "E407", {"position": v(29.54, -22.98) * mm});
            skPoint(sketch, "E408", {"position": v(35.05, -21.49) * mm});
            skPoint(sketch, "E409", {"position": v(35.05, -22.98) * mm});
            skPoint(sketch, "E410", {"position": v(36.56, -21.49) * mm});
            skPoint(sketch, "E411", {"position": v(36.56, -22.98) * mm});
            skPoint(sketch, "E412", {"position": v(40.55, -21.49) * mm});
            skPoint(sketch, "E413", {"position": v(40.55, -22.98) * mm});
            skPoint(sketch, "E414", {"position": v(42.05, -21.49) * mm});
            skPoint(sketch, "E415", {"position": v(42.03, -22.98) * mm});
            skPoint(sketch, "E416", {"position": v(44.25, -21.48) * mm});
            skPoint(sketch, "E417", {"position": v(43.71, -22.98) * mm});
            skPoint(sketch, "E418", {"position": v(40.54, -27.7) * mm});
            skPoint(sketch, "E419", {"position": v(42.03, -26) * mm});
            skPoint(sketch, "E420", {"position": v(16.4, -13.47) * mm});
            skPoint(sketch, "E421", {"position": v(18.54, -11.98) * mm});
            skPoint(sketch, "E422", {"position": v(18.56, -13.52) * mm});
            skPoint(sketch, "E423", {"position": v(20.04, -13.52) * mm});
            skPoint(sketch, "E424", {"position": v(20.04, -11.98) * mm});
            skPoint(sketch, "E425", {"position": v(24.05, -11.98) * mm});
            skPoint(sketch, "E426", {"position": v(24.05, -13.52) * mm});
            skPoint(sketch, "E427", {"position": v(25.57, -12.01) * mm});
            skPoint(sketch, "E428", {"position": v(25.57, -13.5) * mm});
            skPoint(sketch, "E429", {"position": v(29.54, -12.01) * mm});
            skPoint(sketch, "E430", {"position": v(29.54, -13.5) * mm});
            skPoint(sketch, "E431", {"position": v(31.06, -12.01) * mm});
            skPoint(sketch, "E432", {"position": v(31.06, -13.5) * mm});
            skPoint(sketch, "E433", {"position": v(35.08, -12.01) * mm});
            skPoint(sketch, "E434", {"position": v(35.08, -13.5) * mm});
            skPoint(sketch, "E435", {"position": v(36.54, -12.01) * mm});
            skPoint(sketch, "E436", {"position": v(36.54, -13.5) * mm});
            skPoint(sketch, "E437", {"position": v(40.56, -12.01) * mm});
            skPoint(sketch, "E438", {"position": v(40.55, -13.5) * mm});
            skPoint(sketch, "E439", {"position": v(42.05, -13.5) * mm});
            skPoint(sketch, "E440", {"position": v(44.24, -13.5) * mm});
            skPoint(sketch, "E441", {"position": v(42.06, -12.02) * mm});
            skPoint(sketch, "E442", {"position": v(43.72, -12.02) * mm});
            skPoint(sketch, "E443", {"position": v(16.9, -12.01) * mm});
            skPoint(sketch, "E444", {"position": v(20.07, -7.27) * mm});
            skPoint(sketch, "E445", {"position": v(24.05, -4.44) * mm});
            skPoint(sketch, "E446", {"position": v(25.6, -3.8) * mm});
            skPoint(sketch, "E447", {"position": v(29.57, -3.04) * mm});
            skPoint(sketch, "E448", {"position": v(31.07, -3.04) * mm});
            skPoint(sketch, "E449", {"position": v(35.06, -3.8) * mm});
            skPoint(sketch, "E450", {"position": v(36.56, -4.41) * mm});
            skPoint(sketch, "E451", {"position": v(40.57, -7.25) * mm});
            skPoint(sketch, "E452", {"position": v(42.06, -9.01) * mm});
            skPoint(sketch, "E453", {"position": v(30.3, -17.46) * mm});
            skPoint(sketch, "E454", {"position": v(18.57, -21.5) * mm});
            skPoint(sketch, "E455", {"position": v(20.04, -21.5) * mm});
            skLineSegment(sketch, "E456", {"start": v(20.04, -11.98) * mm, "end": v(24.05, -11.98) * mm});
            skLineSegment(sketch, "E457", {"start": v(25.57, -12.01) * mm, "end": v(29.54, -12.01) * mm});
            skLineSegment(sketch, "E458", {"start": v(16.9, -12.01) * mm, "end": v(18.54, -11.98) * mm});
            skLineSegment(sketch, "E459", {"start": v(16.4, -13.47) * mm, "end": v(18.56, -13.52) * mm});
            skLineSegment(sketch, "E460", {"start": v(20.04, -13.52) * mm, "end": v(24.05, -13.52) * mm});
            skLineSegment(sketch, "E461", {"start": v(25.57, -13.5) * mm, "end": v(29.54, -13.5) * mm});
            skLineSegment(sketch, "E462", {"start": v(16.35, -21.45) * mm, "end": v(18.57, -21.5) * mm});
            skLineSegment(sketch, "E463", {"start": v(20.04, -21.5) * mm, "end": v(24.05, -21.49) * mm});
            skLineSegment(sketch, "E464", {"start": v(25.56, -21.49) * mm, "end": v(29.54, -21.49) * mm});
            skLineSegment(sketch, "E465", {"start": v(16.9, -22.98) * mm, "end": v(18.56, -22.98) * mm});
            skLineSegment(sketch, "E466", {"start": v(20.06, -22.98) * mm, "end": v(24.05, -22.98) * mm});
            skLineSegment(sketch, "E467", {"start": v(25.56, -22.98) * mm, "end": v(29.54, -22.98) * mm});
            skLineSegment(sketch, "E468", {"start": v(18.56, -13.52) * mm, "end": v(18.57, -21.5) * mm});
            skLineSegment(sketch, "E469", {"start": v(20.04, -13.52) * mm, "end": v(20.04, -21.5) * mm});
            skLineSegment(sketch, "E470", {"start": v(24.05, -13.52) * mm, "end": v(24.05, -21.49) * mm});
            skLineSegment(sketch, "E471", {"start": v(25.57, -13.5) * mm, "end": v(25.56, -21.49) * mm});
            skLineSegment(sketch, "E472", {"start": v(29.54, -13.5) * mm, "end": v(29.54, -21.49) * mm});
            skLineSegment(sketch, "E473", {"start": v(31.06, -13.5) * mm, "end": v(31.05, -21.49) * mm});
            skArc(sketch, "E474", {"start": v(16.4, -13.47) * mm, "mid": v(15.85, -17.46) * mm, "end": v(16.4, -21.45) * mm});
            skPoint(sketch, "E475", {"position": v(18.56, -9.01) * mm});
            skLineSegment(sketch, "E476", {"start": v(18.56, -9.01) * mm, "end": v(18.54, -11.98) * mm});
            skLineSegment(sketch, "E477", {"start": v(20.07, -7.27) * mm, "end": v(20.04, -11.98) * mm});
            skLineSegment(sketch, "E478", {"start": v(24.05, -4.44) * mm, "end": v(24.05, -11.98) * mm});
            skLineSegment(sketch, "E479", {"start": v(25.6, -3.8) * mm, "end": v(25.57, -12.01) * mm});
            skLineSegment(sketch, "E480", {"start": v(29.57, -3.04) * mm, "end": v(29.54, -12.01) * mm});
            skLineSegment(sketch, "E481", {"start": v(31.07, -3.04) * mm, "end": v(31.06, -12.01) * mm});
            skArc(sketch, "E482", {"start": v(16.9, -12.01) * mm, "mid": v(17.64, -10.47) * mm, "end": v(18.56, -9.01) * mm});
            skArc(sketch, "E483", {"start": v(20.07, -7.27) * mm, "mid": v(21.94, -5.69) * mm, "end": v(24.05, -4.44) * mm});
            skArc(sketch, "E484", {"start": v(25.6, -3.8) * mm, "mid": v(27.56, -3.28) * mm, "end": v(29.57, -3.04) * mm});
            skLineSegment(sketch, "E485", {"start": v(31.06, -12.01) * mm, "end": v(35.08, -12.01) * mm});
            skLineSegment(sketch, "E486", {"start": v(36.54, -12.01) * mm, "end": v(40.56, -12.01) * mm});
            skLineSegment(sketch, "E487", {"start": v(42.06, -12.02) * mm, "end": v(43.72, -12.02) * mm});
            skLineSegment(sketch, "E488", {"start": v(31.06, -13.5) * mm, "end": v(35.08, -13.5) * mm});
            skLineSegment(sketch, "E489", {"start": v(36.54, -13.5) * mm, "end": v(40.55, -13.5) * mm});
            skLineSegment(sketch, "E490", {"start": v(42.05, -13.5) * mm, "end": v(44.24, -13.5) * mm});
            skLineSegment(sketch, "E491", {"start": v(31.05, -21.49) * mm, "end": v(35.05, -21.49) * mm});
            skLineSegment(sketch, "E492", {"start": v(36.56, -21.49) * mm, "end": v(40.55, -21.49) * mm});
            skLineSegment(sketch, "E493", {"start": v(42.05, -21.49) * mm, "end": v(44.25, -21.48) * mm});
            skLineSegment(sketch, "E494", {"start": v(31.05, -22.98) * mm, "end": v(35.05, -22.98) * mm});
            skLineSegment(sketch, "E495", {"start": v(36.56, -22.98) * mm, "end": v(40.55, -22.98) * mm});
            skLineSegment(sketch, "E496", {"start": v(42.03, -22.98) * mm, "end": v(43.71, -22.98) * mm});
            skLineSegment(sketch, "E497", {"start": v(35.08, -13.5) * mm, "end": v(35.05, -21.49) * mm});
            skLineSegment(sketch, "E498", {"start": v(36.54, -13.5) * mm, "end": v(36.56, -21.49) * mm});
            skLineSegment(sketch, "E499", {"start": v(40.55, -13.5) * mm, "end": v(40.55, -21.49) * mm});
            skLineSegment(sketch, "E500", {"start": v(42.05, -13.5) * mm, "end": v(42.05, -21.49) * mm});
            skArc(sketch, "E501", {"start": v(44.24, -13.5) * mm, "mid": v(44.8, -17.49) * mm, "end": v(44.23, -21.48) * mm});
            skLineSegment(sketch, "E502", {"start": v(18.56, -22.98) * mm, "end": v(18.56, -25.97) * mm});
            skLineSegment(sketch, "E503", {"start": v(20.06, -22.98) * mm, "end": v(20.06, -27.74) * mm});
            skLineSegment(sketch, "E504", {"start": v(24.05, -22.98) * mm, "end": v(24.05, -30.56) * mm});
            skLineSegment(sketch, "E505", {"start": v(25.56, -22.98) * mm, "end": v(25.56, -31.17) * mm});
            skLineSegment(sketch, "E506", {"start": v(29.54, -22.98) * mm, "end": v(29.54, -31.95) * mm});
            skLineSegment(sketch, "E507", {"start": v(31.05, -22.98) * mm, "end": v(31.05, -31.95) * mm});
            skLineSegment(sketch, "E508", {"start": v(35.05, -22.98) * mm, "end": v(35.05, -31.17) * mm});
            skLineSegment(sketch, "E509", {"start": v(36.56, -22.98) * mm, "end": v(36.56, -30.56) * mm});
            skLineSegment(sketch, "E510", {"start": v(40.55, -22.98) * mm, "end": v(40.54, -27.7) * mm});
            skLineSegment(sketch, "E511", {"start": v(42.03, -22.98) * mm, "end": v(42.03, -26) * mm});
            skArc(sketch, "E512", {"start": v(43.71, -22.98) * mm, "mid": v(42.96, -24.54) * mm, "end": v(42.03, -26) * mm});
            skArc(sketch, "E513", {"start": v(40.54, -27.7) * mm, "mid": v(38.67, -29.28) * mm, "end": v(36.56, -30.52) * mm});
            skArc(sketch, "E514", {"start": v(35.05, -31.17) * mm, "mid": v(33.08, -31.7) * mm, "end": v(31.05, -31.95) * mm});
            skArc(sketch, "E515", {"start": v(29.54, -31.95) * mm, "mid": v(38.72, -29.28) * mm, "end": v(44.25, -21.48) * mm});
            skArc(sketch, "E516", {"start": v(16.9, -22.98) * mm, "mid": v(17.64, -24.52) * mm, "end": v(18.56, -25.97) * mm});
            skArc(sketch, "E517", {"start": v(20.06, -27.74) * mm, "mid": v(21.94, -29.32) * mm, "end": v(24.05, -30.56) * mm});
            skArc(sketch, "E518", {"start": v(25.56, -31.17) * mm, "mid": v(27.52, -31.7) * mm, "end": v(29.54, -31.95) * mm});
            skLineSegment(sketch, "E519", {"start": v(35.06, -3.8) * mm, "end": v(35.08, -12.01) * mm});
            skLineSegment(sketch, "E520", {"start": v(36.56, -4.41) * mm, "end": v(36.54, -12.01) * mm});
            skLineSegment(sketch, "E521", {"start": v(40.57, -7.25) * mm, "end": v(40.56, -12.01) * mm});
            skLineSegment(sketch, "E522", {"start": v(42.06, -9.01) * mm, "end": v(42.06, -12.02) * mm});
            skArc(sketch, "E523", {"start": v(31.07, -3.04) * mm, "mid": v(33.1, -3.29) * mm, "end": v(35.06, -3.82) * mm});
            skArc(sketch, "E524", {"start": v(36.56, -4.41) * mm, "mid": v(38.68, -5.66) * mm, "end": v(40.57, -7.26) * mm});
            skArc(sketch, "E525", {"start": v(42.06, -9.01) * mm, "mid": v(42.98, -10.46) * mm, "end": v(43.72, -12.02) * mm});
            skPoint(sketch, "E526", {"position": v(16.9, 12.05) * mm});
            skPoint(sketch, "E527", {"position": v(16.37, 13.52) * mm});
            skPoint(sketch, "E528", {"position": v(18.55, 13.5) * mm});
            skPoint(sketch, "E529", {"position": v(18.55, 12.05) * mm});
            skPoint(sketch, "E530", {"position": v(20.07, 12.05) * mm});
            skPoint(sketch, "E531", {"position": v(20.07, 13.5) * mm});
            skPoint(sketch, "E532", {"position": v(18.55, 9.04) * mm});
            skPoint(sketch, "E533", {"position": v(20.06, 7.25) * mm});
            skPoint(sketch, "E534", {"position": v(24.06, 4.42) * mm});
            skPoint(sketch, "E535", {"position": v(25.56, 3.83) * mm});
            skPoint(sketch, "E536", {"position": v(29.56, 3.05) * mm});
            skPoint(sketch, "E537", {"position": v(31.06, 3.06) * mm});
            skPoint(sketch, "E538", {"position": v(35.06, 3.81) * mm});
            skPoint(sketch, "E539", {"position": v(36.56, 4.42) * mm});
            skPoint(sketch, "E540", {"position": v(40.56, 7.24) * mm});
            skPoint(sketch, "E541", {"position": v(42.06, 9.03) * mm});
            skPoint(sketch, "E542", {"position": v(42.05, 12.05) * mm});
            skPoint(sketch, "E543", {"position": v(40.56, 12.05) * mm});
            skPoint(sketch, "E544", {"position": v(36.53, 12.05) * mm});
            skPoint(sketch, "E545", {"position": v(35.04, 12.05) * mm});
            skPoint(sketch, "E546", {"position": v(43.73, 12.05) * mm});
            skPoint(sketch, "E547", {"position": v(44.23, 13.49) * mm});
            skPoint(sketch, "E548", {"position": v(42.04, 13.47) * mm});
            skPoint(sketch, "E549", {"position": v(40.54, 13.47) * mm});
            skPoint(sketch, "E550", {"position": v(36.53, 13.47) * mm});
            skPoint(sketch, "E551", {"position": v(35.03, 13.47) * mm});
            skPoint(sketch, "E552", {"position": v(31.07, 13.47) * mm});
            skPoint(sketch, "E553", {"position": v(31.05, 12.04) * mm});
            skPoint(sketch, "E554", {"position": v(24.06, 13.5) * mm});
            skPoint(sketch, "E555", {"position": v(25.56, 13.5) * mm});
            skPoint(sketch, "E556", {"position": v(29.57, 13.5) * mm});
            skPoint(sketch, "E557", {"position": v(24.06, 12.07) * mm});
            skPoint(sketch, "E558", {"position": v(25.56, 12.07) * mm});
            skPoint(sketch, "E559", {"position": v(29.55, 12.06) * mm});
            skPoint(sketch, "E560", {"position": v(16.38, 21.5) * mm});
            skPoint(sketch, "E561", {"position": v(18.56, 21.5) * mm});
            skPoint(sketch, "E562", {"position": v(20.06, 21.57) * mm});
            skPoint(sketch, "E563", {"position": v(24.06, 21.57) * mm});
            skPoint(sketch, "E564", {"position": v(25.56, 21.57) * mm});
            skPoint(sketch, "E565", {"position": v(29.56, 21.57) * mm});
            skPoint(sketch, "E566", {"position": v(31.06, 21.57) * mm});
            skPoint(sketch, "E567", {"position": v(35.04, 21.57) * mm});
            skPoint(sketch, "E568", {"position": v(36.55, 21.57) * mm});
            skPoint(sketch, "E569", {"position": v(40.55, 21.57) * mm});
            skPoint(sketch, "E570", {"position": v(42.05, 21.57) * mm});
            skPoint(sketch, "E571", {"position": v(44.23, 21.57) * mm});
            skPoint(sketch, "E572", {"position": v(43.68, 23.07) * mm});
            skPoint(sketch, "E573", {"position": v(18.55, 25.97) * mm});
            skPoint(sketch, "E574", {"position": v(20.07, 27.77) * mm});
            skPoint(sketch, "E575", {"position": v(24.06, 30.59) * mm});
            skPoint(sketch, "E576", {"position": v(29.56, 31.98) * mm});
            skPoint(sketch, "E577", {"position": v(25.56, 31.2) * mm});
            skPoint(sketch, "E578", {"position": v(30.98, 31.98) * mm});
            skPoint(sketch, "E579", {"position": v(36.57, 30.59) * mm});
            skPoint(sketch, "E580", {"position": v(40.56, 27.77) * mm});
            skPoint(sketch, "E581", {"position": v(42.07, 25.97) * mm});
            skLineSegment(sketch, "E582", {"start": v(20.06, 23.06) * mm, "end": v(24.06, 23.06) * mm});
            skLineSegment(sketch, "E583", {"start": v(25.56, 23.06) * mm, "end": v(29.56, 23.05) * mm});
            skLineSegment(sketch, "E584", {"start": v(16.38, 21.5) * mm, "end": v(18.56, 21.5) * mm});
            skLineSegment(sketch, "E585", {"start": v(20.06, 21.57) * mm, "end": v(24.06, 21.57) * mm});
            skLineSegment(sketch, "E586", {"start": v(25.56, 21.57) * mm, "end": v(29.56, 21.57) * mm});
            skLineSegment(sketch, "E587", {"start": v(31.06, 23.05) * mm, "end": v(35.06, 23.06) * mm});
            skLineSegment(sketch, "E588", {"start": v(36.56, 23.06) * mm, "end": v(40.56, 23.05) * mm});
            skLineSegment(sketch, "E589", {"start": v(31.06, 21.57) * mm, "end": v(35.04, 21.57) * mm});
            skLineSegment(sketch, "E590", {"start": v(36.55, 21.57) * mm, "end": v(40.55, 21.57) * mm});
            skLineSegment(sketch, "E591", {"start": v(18.55, 25.97) * mm, "end": v(18.56, 23.06) * mm});
            skLineSegment(sketch, "E592", {"start": v(20.07, 27.77) * mm, "end": v(20.06, 23.06) * mm});
            skLineSegment(sketch, "E593", {"start": v(24.06, 30.59) * mm, "end": v(24.06, 23.06) * mm});
            skLineSegment(sketch, "E594", {"start": v(25.56, 31.2) * mm, "end": v(25.56, 23.06) * mm});
            skLineSegment(sketch, "E595", {"start": v(29.56, 31.98) * mm, "end": v(29.56, 23.05) * mm});
            skLineSegment(sketch, "E596", {"start": v(30.98, 31.98) * mm, "end": v(31.06, 23.05) * mm});
            skLineSegment(sketch, "E597", {"start": v(35.07, 31.2) * mm, "end": v(35.06, 23.06) * mm});
            skLineSegment(sketch, "E598", {"start": v(36.57, 30.59) * mm, "end": v(36.56, 23.06) * mm});
            skLineSegment(sketch, "E599", {"start": v(40.56, 27.77) * mm, "end": v(40.56, 23.05) * mm});
            skLineSegment(sketch, "E600", {"start": v(42.07, 25.97) * mm, "end": v(42.06, 23.06) * mm});
            skLineSegment(sketch, "E601", {"start": v(42.05, 21.57) * mm, "end": v(44.23, 21.57) * mm});
            skLineSegment(sketch, "E602", {"start": v(16.37, 13.52) * mm, "end": v(18.55, 13.5) * mm});
            skLineSegment(sketch, "E603", {"start": v(18.56, 21.5) * mm, "end": v(18.55, 13.5) * mm});
            skLineSegment(sketch, "E604", {"start": v(20.06, 21.57) * mm, "end": v(20.07, 13.5) * mm});
            skLineSegment(sketch, "E605", {"start": v(24.06, 13.5) * mm, "end": v(24.06, 21.57) * mm});
            skLineSegment(sketch, "E606", {"start": v(25.56, 21.57) * mm, "end": v(25.56, 13.5) * mm});
            skLineSegment(sketch, "E607", {"start": v(29.57, 13.5) * mm, "end": v(29.56, 21.57) * mm});
            skLineSegment(sketch, "E608", {"start": v(31.06, 21.57) * mm, "end": v(31.07, 13.47) * mm});
            skLineSegment(sketch, "E609", {"start": v(35.03, 13.47) * mm, "end": v(35.04, 21.57) * mm});
            skLineSegment(sketch, "E610", {"start": v(36.55, 21.57) * mm, "end": v(36.53, 13.47) * mm});
            skLineSegment(sketch, "E611", {"start": v(40.54, 13.47) * mm, "end": v(40.55, 21.57) * mm});
            skLineSegment(sketch, "E612", {"start": v(42.05, 21.57) * mm, "end": v(42.04, 13.47) * mm});
            skLineSegment(sketch, "E613", {"start": v(16.9, 12.05) * mm, "end": v(18.55, 12.05) * mm});
            skLineSegment(sketch, "E614", {"start": v(18.55, 12.05) * mm, "end": v(18.55, 9.04) * mm});
            skLineSegment(sketch, "E615", {"start": v(20.07, 12.05) * mm, "end": v(24.06, 12.07) * mm});
            skLineSegment(sketch, "E616", {"start": v(25.56, 12.07) * mm, "end": v(29.55, 12.06) * mm});
            skLineSegment(sketch, "E617", {"start": v(31.05, 12.04) * mm, "end": v(35.04, 12.05) * mm});
            skLineSegment(sketch, "E618", {"start": v(36.53, 12.05) * mm, "end": v(40.56, 12.05) * mm});
            skLineSegment(sketch, "E619", {"start": v(42.05, 12.05) * mm, "end": v(43.73, 12.05) * mm});
            skLineSegment(sketch, "E620", {"start": v(42.05, 12.05) * mm, "end": v(42.06, 9.03) * mm});
            skLineSegment(sketch, "E621", {"start": v(20.07, 12.05) * mm, "end": v(20.06, 7.25) * mm});
            skLineSegment(sketch, "E622", {"start": v(24.06, 12.07) * mm, "end": v(24.06, 4.42) * mm});
            skLineSegment(sketch, "E623", {"start": v(25.56, 12.07) * mm, "end": v(25.56, 3.83) * mm});
            skLineSegment(sketch, "E624", {"start": v(29.55, 12.06) * mm, "end": v(29.56, 3.05) * mm});
            skLineSegment(sketch, "E625", {"start": v(31.05, 12.04) * mm, "end": v(31.06, 3.06) * mm});
            skLineSegment(sketch, "E626", {"start": v(35.04, 12.05) * mm, "end": v(35.06, 3.81) * mm});
            skLineSegment(sketch, "E627", {"start": v(36.53, 12.05) * mm, "end": v(36.56, 4.42) * mm});
            skLineSegment(sketch, "E628", {"start": v(40.56, 12.05) * mm, "end": v(40.56, 7.24) * mm});
            skArc(sketch, "E629", {"start": v(20.07, 27.77) * mm, "mid": v(21.95, 29.35) * mm, "end": v(24.06, 30.59) * mm});
            skArc(sketch, "E630", {"start": v(25.56, 31.2) * mm, "mid": v(27.53, 31.72) * mm, "end": v(29.56, 31.97) * mm});
            skArc(sketch, "E631", {"start": v(30.98, 31.98) * mm, "mid": v(33.05, 31.73) * mm, "end": v(35.07, 31.2) * mm});
            skArc(sketch, "E632", {"start": v(36.57, 30.59) * mm, "mid": v(38.68, 29.35) * mm, "end": v(40.56, 27.76) * mm});
            skArc(sketch, "E633", {"start": v(42.07, 25.97) * mm, "mid": v(42.96, 24.57) * mm, "end": v(43.68, 23.07) * mm});
            skArc(sketch, "E634", {"start": v(16.38, 21.5) * mm, "mid": v(15.82, 17.51) * mm, "end": v(16.39, 13.52) * mm});
            skArc(sketch, "E635", {"start": v(44.23, 21.57) * mm, "mid": v(44.8, 17.53) * mm, "end": v(44.23, 13.49) * mm});
            skArc(sketch, "E636", {"start": v(43.73, 12.05) * mm, "mid": v(42.98, 10.5) * mm, "end": v(42.06, 9.04) * mm});
            skArc(sketch, "E637", {"start": v(40.56, 7.24) * mm, "mid": v(38.68, 5.66) * mm, "end": v(36.56, 4.42) * mm});
            skArc(sketch, "E638", {"start": v(16.9, 12.05) * mm, "mid": v(17.64, 10.5) * mm, "end": v(18.55, 9.06) * mm});
            skArc(sketch, "E639", {"start": v(20.06, 7.25) * mm, "mid": v(21.94, 5.66) * mm, "end": v(24.06, 4.42) * mm});
            skArc(sketch, "E640", {"start": v(25.56, 3.83) * mm, "mid": v(27.53, 3.3) * mm, "end": v(29.56, 3.05) * mm});
            skArc(sketch, "E641", {"start": v(31.06, 3.06) * mm, "mid": v(33.09, 3.31) * mm, "end": v(35.06, 3.84) * mm});
            skLineSegment(sketch, "E642", {"start": v(20.07, 13.5) * mm, "end": v(24.06, 13.5) * mm});
            skLineSegment(sketch, "E643", {"start": v(25.56, 13.5) * mm, "end": v(29.57, 13.5) * mm});
            skLineSegment(sketch, "E644", {"start": v(31.07, 13.47) * mm, "end": v(35.03, 13.47) * mm});
            skLineSegment(sketch, "E645", {"start": v(36.53, 13.47) * mm, "end": v(40.54, 13.47) * mm});
            skLineSegment(sketch, "E646", {"start": v(42.04, 13.47) * mm, "end": v(44.23, 13.49) * mm});
            skLineSegment(sketch, "E647", {"start": v(42.06, 23.06) * mm, "end": v(43.68, 23.07) * mm});
            skPoint(sketch, "E648", {"position": v(16.94, 23.06) * mm});
            skLineSegment(sketch, "E649", {"start": v(16.94, 23.06) * mm, "end": v(18.56, 23.06) * mm});
            skArc(sketch, "E650", {"start": v(16.94, 23.06) * mm, "mid": v(17.66, 24.56) * mm, "end": v(18.55, 25.96) * mm});
            skSolve(sketch);
        }
        {
            var Q0;
            Q0=makeQuery(id+"F1.imprint","IMPRINT",FACE,{"disambiguationData":[TD([[makeQuery(id+"F1.imprint","IMPRINT",EDGE,{"derivedFrom":sQuery(id+"F1.wireOp",EDGE,"E143.bottom")}),1.0]])]});
            extrude(context, id + "F2", {"entities" : qUnion([Q0]), "depth" : 4 * mm, "offsetDistance" : 25 * mm});
        }
        {
            var Q0;
            {var subQ0=sQuery(id+"F0.wireOp",EDGE,"E20");var subQ1=sQuery(id+"F0.wireOp",EDGE,"QIJiGY5w-lFCi-xx9X-rp0q-5GBFziIUs7mU");var subQ2=makeQuery(id+"F0.imprint","INTERSECT",VERTEX,{"disambiguationData":[OD(0.0)],"derivedFrom":[subQ1,subQ0]});Q0=makeQuery(id+"F0.imprint","IMPRINT",FACE,{"disambiguationData":[TD([[makeQuery(id+"F0.imprint","IMPRINT",EDGE,{"disambiguationData":[TD([[subQ2,-1.0]])],"derivedFrom":subQ1}),-1.0]])]});}
            var Q1;
            {var subQ0=sQuery(id+"F0.wireOp",EDGE,"E21");var subQ1=sQuery(id+"F0.wireOp",EDGE,"E5");var subQ2=makeQuery(id+"F0.imprint","INTERSECT",VERTEX,{"disambiguationData":[OD(0.0)],"derivedFrom":[subQ1,subQ0]});Q1=makeQuery(id+"F0.imprint","IMPRINT",FACE,{"disambiguationData":[TD([[makeQuery(id+"F0.imprint","IMPRINT",EDGE,{"disambiguationData":[TD([[subQ2,-1.0]])],"derivedFrom":subQ1}),1.0]])]});}
            var Q2;
            {var subQ0=sQuery(id+"F0.wireOp",EDGE,"E21");var subQ1=sQuery(id+"F0.wireOp",EDGE,"E5");var subQ2=makeQuery(id+"F0.imprint","INTERSECT",VERTEX,{"disambiguationData":[OD(0.0)],"derivedFrom":[subQ1,subQ0]});Q2=makeQuery(id+"F0.imprint","IMPRINT",FACE,{"disambiguationData":[TD([[makeQuery(id+"F0.imprint","IMPRINT",EDGE,{"disambiguationData":[TD([[subQ2,-1.0]])],"derivedFrom":subQ1}),-1.0]])]});}
            var Q3;
            {var subQ0=sQuery(id+"F0.wireOp",EDGE,"E22");var subQ1=sQuery(id+"F0.wireOp",EDGE,"b7w3sZkz-h2S3-PTXa-qy05-PL4N3AHQH3GV");var subQ2=makeQuery(id+"F0.imprint","INTERSECT",VERTEX,{"disambiguationData":[OD(0.0)],"derivedFrom":[subQ1,subQ0]});Q3=makeQuery(id+"F0.imprint","IMPRINT",FACE,{"disambiguationData":[TD([[makeQuery(id+"F0.imprint","IMPRINT",EDGE,{"disambiguationData":[TD([[subQ2,-1.0]])],"derivedFrom":subQ1}),-1.0]])]});}
            var Q4;
            {var subQ0=sQuery(id+"F0.wireOp",EDGE,"E5");var subQ1=sQuery(id+"F0.wireOp",EDGE,"b7w3sZkz-h2S3-PTXa-qy05-PL4N3AHQH3GV");var subQ2=makeQuery(id+"F0.imprint","INTERSECT",VERTEX,{"disambiguationData":[OD(0.0)],"derivedFrom":[subQ1,subQ0]});Q4=makeQuery(id+"F0.imprint","IMPRINT",FACE,{"disambiguationData":[TD([[makeQuery(id+"F0.imprint","IMPRINT",EDGE,{"disambiguationData":[TD([[subQ2,-1.0]])],"derivedFrom":subQ1}),-1.0]])]});}
            var Q5;
            {var subQ0=sQuery(id+"F0.wireOp",EDGE,"E5");var subQ1=sQuery(id+"F0.wireOp",EDGE,"b7w3sZkz-h2S3-PTXa-qy05-PL4N3AHQH3GV");var subQ2=makeQuery(id+"F0.imprint","INTERSECT",VERTEX,{"disambiguationData":[OD(0.0)],"derivedFrom":[subQ1,subQ0]});Q5=makeQuery(id+"F0.imprint","IMPRINT",FACE,{"disambiguationData":[TD([[makeQuery(id+"F0.imprint","IMPRINT",EDGE,{"disambiguationData":[TD([[subQ2,-1.0]])],"derivedFrom":subQ1}),1.0]])]});}
            var Q6;
            {var subQ0=sQuery(id+"F0.wireOp",EDGE,"E22");var subQ1=sQuery(id+"F0.wireOp",EDGE,"b7w3sZkz-h2S3-PTXa-qy05-PL4N3AHQH3GV");var subQ2=makeQuery(id+"F0.imprint","INTERSECT",VERTEX,{"disambiguationData":[OD(0.0)],"derivedFrom":[subQ1,subQ0]});Q6=makeQuery(id+"F0.imprint","IMPRINT",FACE,{"disambiguationData":[TD([[makeQuery(id+"F0.imprint","IMPRINT",EDGE,{"disambiguationData":[TD([[subQ2,-1.0]])],"derivedFrom":subQ1}),1.0]])]});}
            var Q7;
            {var subQ0=sQuery(id+"F0.wireOp",EDGE,"E23");var subQ1=sQuery(id+"F0.wireOp",EDGE,"QIJiGY5w-lFCi-xx9X-rp0q-5GBFziIUs7mU");var subQ2=makeQuery(id+"F0.imprint","INTERSECT",VERTEX,{"disambiguationData":[OD(0.0)],"derivedFrom":[subQ1,subQ0]});Q7=makeQuery(id+"F0.imprint","IMPRINT",FACE,{"disambiguationData":[TD([[makeQuery(id+"F0.imprint","IMPRINT",EDGE,{"disambiguationData":[TD([[subQ2,-1.0]])],"derivedFrom":subQ1}),1.0]])]});}
            var Q8;
            {var subQ0=sQuery(id+"F0.wireOp",EDGE,"E5");var subQ1=sQuery(id+"F0.wireOp",EDGE,"QIJiGY5w-lFCi-xx9X-rp0q-5GBFziIUs7mU");var subQ2=makeQuery(id+"F0.imprint","INTERSECT",VERTEX,{"disambiguationData":[OD(1.0)],"derivedFrom":[subQ1,subQ0]});Q8=makeQuery(id+"F0.imprint","IMPRINT",FACE,{"disambiguationData":[TD([[makeQuery(id+"F0.imprint","IMPRINT",EDGE,{"disambiguationData":[TD([[subQ2,-1.0]])],"derivedFrom":subQ1}),1.0]])]});}
            var Q9;
            {var subQ0=sQuery(id+"F0.wireOp",EDGE,"E5");var subQ1=sQuery(id+"F0.wireOp",EDGE,"QIJiGY5w-lFCi-xx9X-rp0q-5GBFziIUs7mU");var subQ2=makeQuery(id+"F0.imprint","INTERSECT",VERTEX,{"disambiguationData":[OD(1.0)],"derivedFrom":[subQ1,subQ0]});Q9=makeQuery(id+"F0.imprint","IMPRINT",FACE,{"disambiguationData":[TD([[makeQuery(id+"F0.imprint","IMPRINT",EDGE,{"disambiguationData":[TD([[subQ2,-1.0]])],"derivedFrom":subQ1}),-1.0]])]});}
            var Q10;
            {var subQ0=sQuery(id+"F0.wireOp",EDGE,"E23");var subQ1=sQuery(id+"F0.wireOp",EDGE,"QIJiGY5w-lFCi-xx9X-rp0q-5GBFziIUs7mU");var subQ2=makeQuery(id+"F0.imprint","INTERSECT",VERTEX,{"disambiguationData":[OD(0.0)],"derivedFrom":[subQ1,subQ0]});Q10=makeQuery(id+"F0.imprint","IMPRINT",FACE,{"disambiguationData":[TD([[makeQuery(id+"F0.imprint","IMPRINT",EDGE,{"disambiguationData":[TD([[subQ2,-1.0]])],"derivedFrom":subQ1}),-1.0]])]});}
            var Q11;
            {var subQ0=sQuery(id+"F0.wireOp",EDGE,"E24");var subQ1=sQuery(id+"F0.wireOp",EDGE,"E5");var subQ2=makeQuery(id+"F0.imprint","INTERSECT",VERTEX,{"disambiguationData":[OD(0.0)],"derivedFrom":[subQ1,subQ0]});Q11=makeQuery(id+"F0.imprint","IMPRINT",FACE,{"disambiguationData":[TD([[makeQuery(id+"F0.imprint","IMPRINT",EDGE,{"disambiguationData":[TD([[subQ2,-1.0]])],"derivedFrom":subQ1}),-1.0]])]});}
            var Q12;
            {var subQ0=sQuery(id+"F0.wireOp",EDGE,"E24");var subQ1=sQuery(id+"F0.wireOp",EDGE,"E5");var subQ2=makeQuery(id+"F0.imprint","INTERSECT",VERTEX,{"disambiguationData":[OD(0.0)],"derivedFrom":[subQ1,subQ0]});Q12=makeQuery(id+"F0.imprint","IMPRINT",FACE,{"disambiguationData":[TD([[makeQuery(id+"F0.imprint","IMPRINT",EDGE,{"disambiguationData":[TD([[subQ2,-1.0]])],"derivedFrom":subQ1}),1.0]])]});}
            var Q13;
            {var subQ0=sQuery(id+"F0.wireOp",EDGE,"E19");var subQ1=sQuery(id+"F0.wireOp",EDGE,"QIJiGY5w-lFCi-xx9X-rp0q-5GBFziIUs7mU");var subQ2=makeQuery(id+"F0.imprint","INTERSECT",VERTEX,{"disambiguationData":[OD(0.0)],"derivedFrom":[subQ1,subQ0]});Q13=makeQuery(id+"F0.imprint","IMPRINT",FACE,{"disambiguationData":[TD([[makeQuery(id+"F0.imprint","IMPRINT",EDGE,{"disambiguationData":[TD([[subQ2,-1.0]])],"derivedFrom":subQ1}),1.0]])]});}
            var Q14;
            {var subQ0=sQuery(id+"F0.wireOp",EDGE,"E19");var subQ1=sQuery(id+"F0.wireOp",EDGE,"QIJiGY5w-lFCi-xx9X-rp0q-5GBFziIUs7mU");var subQ2=makeQuery(id+"F0.imprint","INTERSECT",VERTEX,{"disambiguationData":[OD(0.0)],"derivedFrom":[subQ1,subQ0]});Q14=makeQuery(id+"F0.imprint","IMPRINT",FACE,{"disambiguationData":[TD([[makeQuery(id+"F0.imprint","IMPRINT",EDGE,{"disambiguationData":[TD([[subQ2,-1.0]])],"derivedFrom":subQ1}),-1.0]])]});}
            var Q15;
            {var subQ0=sQuery(id+"F0.wireOp",EDGE,"b7w3sZkz-h2S3-PTXa-qy05-PL4N3AHQH3GV");var subQ1=sQuery(id+"F0.wireOp",EDGE,"QIJiGY5w-lFCi-xx9X-rp0q-5GBFziIUs7mU");var subQ2=makeQuery(id+"F0.imprint","INTERSECT",VERTEX,{"derivedFrom":[subQ1,subQ0]});Q15=makeQuery(id+"F0.imprint","IMPRINT",FACE,{"disambiguationData":[TD([[makeQuery(id+"F0.imprint","IMPRINT",EDGE,{"disambiguationData":[TD([[subQ2,-1.0]])],"derivedFrom":subQ1}),-1.0]])]});}
            var Q16;
            {var subQ0=sQuery(id+"F0.wireOp",EDGE,"b7w3sZkz-h2S3-PTXa-qy05-PL4N3AHQH3GV");var subQ1=sQuery(id+"F0.wireOp",EDGE,"QIJiGY5w-lFCi-xx9X-rp0q-5GBFziIUs7mU");var subQ2=makeQuery(id+"F0.imprint","INTERSECT",VERTEX,{"derivedFrom":[subQ1,subQ0]});Q16=makeQuery(id+"F0.imprint","IMPRINT",FACE,{"disambiguationData":[TD([[makeQuery(id+"F0.imprint","IMPRINT",EDGE,{"disambiguationData":[TD([[subQ2,-1.0]])],"derivedFrom":subQ1}),1.0]])]});}
            var Q17;
            Q17=makeQuery(id+"F0.imprint","IMPRINT",FACE,{"disambiguationData":[TD([[makeQuery(id+"F0.imprint","IMPRINT",EDGE,{"derivedFrom":sQuery(id+"F0.wireOp",EDGE,"E28")}),-1.0]])]});
            var Q18;
            Q18=makeQuery(id+"F0.imprint","IMPRINT",FACE,{"disambiguationData":[TD([[makeQuery(id+"F0.imprint","IMPRINT",EDGE,{"derivedFrom":sQuery(id+"F0.wireOp",EDGE,"E37")}),1.0]])]});
            var Q19;
            Q19=makeQuery(id+"F0.imprint","IMPRINT",FACE,{"disambiguationData":[TD([[makeQuery(id+"F0.imprint","IMPRINT",EDGE,{"derivedFrom":sQuery(id+"F0.wireOp",EDGE,"E40")}),-1.0]])]});
            var Q20;
            Q20=makeQuery(id+"F0.imprint","IMPRINT",FACE,{"disambiguationData":[TD([[makeQuery(id+"F0.imprint","IMPRINT",EDGE,{"derivedFrom":sQuery(id+"F0.wireOp",EDGE,"E43")}),-1.0]])]});
            var Q21;
            Q21=makeQuery(id+"F0.imprint","IMPRINT",FACE,{"disambiguationData":[TD([[makeQuery(id+"F0.imprint","IMPRINT",EDGE,{"derivedFrom":sQuery(id+"F0.wireOp",EDGE,"E32")}),1.0]])]});
            var Q22;
            Q22=makeQuery(id+"F0.imprint","IMPRINT",FACE,{"disambiguationData":[TD([[makeQuery(id+"F0.imprint","IMPRINT",EDGE,{"derivedFrom":sQuery(id+"F0.wireOp",EDGE,"E35")}),1.0]])]});
            var Q23;
            Q23=makeQuery(id+"F1.imprint","IMPRINT",FACE,{"disambiguationData":[TD([[makeQuery(id+"F1.imprint","IMPRINT",EDGE,{"derivedFrom":sQuery(id+"F1.wireOp",EDGE,"E601")}),-1.0]])]});
            extrude(context, id + "F3", {"entities" : qUnion([Q0, Q1, Q2, Q3, Q4, Q5, Q6, Q7, Q8, Q9, Q10, Q11, Q12, Q13, Q14, Q15, Q16, Q17, Q18, Q19, Q20, Q21, Q22, Q23]), "operationType" : NewBodyOperationType.ADD, "depth" : 4 * mm, "offsetDistance" : 25 * mm});
        }
        {
            var Q0;
            {var subQ0=sQuery(id+"F0.wireOp",EDGE,"E10");var subQ1=sQuery(id+"F0.wireOp",EDGE,"QIJiGY5w-lFCi-xx9X-rp0q-5GBFziIUs7mU");var subQ2=makeQuery(id+"F0.imprint","INTERSECT",VERTEX,{"derivedFrom":[subQ1,subQ0]});Q0=makeQuery(id+"F0.imprint","IMPRINT",FACE,{"disambiguationData":[TD([[makeQuery(id+"F0.imprint","IMPRINT",EDGE,{"disambiguationData":[TD([[subQ2,-1.0]])],"derivedFrom":subQ1}),1.0]])]});}
            var Q1;
            {var subQ0=sQuery(id+"F0.wireOp",EDGE,"E10");var subQ1=sQuery(id+"F0.wireOp",EDGE,"QIJiGY5w-lFCi-xx9X-rp0q-5GBFziIUs7mU");var subQ2=makeQuery(id+"F0.imprint","INTERSECT",VERTEX,{"derivedFrom":[subQ1,subQ0]});Q1=makeQuery(id+"F0.imprint","IMPRINT",FACE,{"disambiguationData":[TD([[makeQuery(id+"F0.imprint","IMPRINT",EDGE,{"disambiguationData":[TD([[subQ2,-1.0]])],"derivedFrom":subQ1}),-1.0]])]});}
            var Q2;
            {var subQ0=sQuery(id+"F0.wireOp",EDGE,"E10");var subQ1=sQuery(id+"F0.wireOp",EDGE,"E5");var subQ2=makeQuery(id+"F0.imprint","INTERSECT",VERTEX,{"disambiguationData":[OD(1.0)],"derivedFrom":[subQ1,subQ0]});Q2=makeQuery(id+"F0.imprint","IMPRINT",FACE,{"disambiguationData":[TD([[makeQuery(id+"F0.imprint","IMPRINT",EDGE,{"disambiguationData":[TD([[subQ2,1.0]])],"derivedFrom":subQ1}),1.0]])]});}
            var Q3;
            {var subQ0=sQuery(id+"F0.wireOp",EDGE,"E10");var subQ4=sQuery(id+"F0.wireOp",EDGE,"E5");var subQ5=makeQuery(id+"F0.imprint","INTERSECT",VERTEX,{"disambiguationData":[OD(0.0)],"derivedFrom":[subQ4,subQ0]});Q3=makeQuery(id+"F0.imprint","IMPRINT",FACE,{"disambiguationData":[TD([[makeQuery(id+"F0.imprint","IMPRINT",EDGE,{"disambiguationData":[TD([[subQ5,-1.0]])],"derivedFrom":subQ4}),1.0]])]});}
            var Q4;
            {var subQ0=sQuery(id+"F0.wireOp",EDGE,"E17");var subQ3=sQuery(id+"F0.wireOp",EDGE,"E5");var subQ7=makeQuery(id+"F0.imprint","INTERSECT",VERTEX,{"disambiguationData":[OD(0.0)],"derivedFrom":[subQ3,subQ0]});Q4=makeQuery(id+"F0.imprint","IMPRINT",FACE,{"disambiguationData":[TD([[makeQuery(id+"F0.imprint","IMPRINT",EDGE,{"disambiguationData":[TD([[subQ7,-1.0]])],"derivedFrom":subQ3}),1.0]])]});}
            var Q5;
            {var subQ0=sQuery(id+"F0.wireOp",EDGE,"E17");var subQ1=sQuery(id+"F0.wireOp",EDGE,"E5");var subQ2=makeQuery(id+"F0.imprint","INTERSECT",VERTEX,{"disambiguationData":[OD(0.0)],"derivedFrom":[subQ1,subQ0]});Q5=makeQuery(id+"F0.imprint","IMPRINT",FACE,{"disambiguationData":[TD([[makeQuery(id+"F0.imprint","IMPRINT",EDGE,{"disambiguationData":[TD([[subQ2,-1.0]])],"derivedFrom":subQ1}),-1.0]])]});}
            var Q6;
            {var subQ0=sQuery(id+"F0.wireOp",EDGE,"E11");var subQ1=sQuery(id+"F0.wireOp",EDGE,"b7w3sZkz-h2S3-PTXa-qy05-PL4N3AHQH3GV");var subQ2=makeQuery(id+"F0.imprint","INTERSECT",VERTEX,{"derivedFrom":[subQ1,subQ0]});Q6=makeQuery(id+"F0.imprint","IMPRINT",FACE,{"disambiguationData":[TD([[makeQuery(id+"F0.imprint","IMPRINT",EDGE,{"disambiguationData":[TD([[subQ2,-1.0]])],"derivedFrom":subQ1}),-1.0]])]});}
            var Q7;
            {var subQ0=sQuery(id+"F0.wireOp",EDGE,"E11");var subQ1=sQuery(id+"F0.wireOp",EDGE,"b7w3sZkz-h2S3-PTXa-qy05-PL4N3AHQH3GV");var subQ2=makeQuery(id+"F0.imprint","INTERSECT",VERTEX,{"derivedFrom":[subQ1,subQ0]});Q7=makeQuery(id+"F0.imprint","IMPRINT",FACE,{"disambiguationData":[TD([[makeQuery(id+"F0.imprint","IMPRINT",EDGE,{"disambiguationData":[TD([[subQ2,-1.0]])],"derivedFrom":subQ1}),1.0]])]});}
            var Q8;
            {var subQ0=sQuery(id+"F0.wireOp",EDGE,"E11");var subQ1=sQuery(id+"F0.wireOp",EDGE,"E5");var subQ2=makeQuery(id+"F0.imprint","INTERSECT",VERTEX,{"disambiguationData":[OD(0.0)],"derivedFrom":[subQ1,subQ0]});Q8=makeQuery(id+"F0.imprint","IMPRINT",FACE,{"disambiguationData":[TD([[makeQuery(id+"F0.imprint","IMPRINT",EDGE,{"disambiguationData":[TD([[subQ2,-1.0]])],"derivedFrom":subQ1}),1.0]])]});}
            var Q9;
            {var subQ0=sQuery(id+"F0.wireOp",EDGE,"E11");var subQ1=sQuery(id+"F0.wireOp",EDGE,"E5");var subQ2=makeQuery(id+"F0.imprint","INTERSECT",VERTEX,{"disambiguationData":[OD(1.0)],"derivedFrom":[subQ1,subQ0]});Q9=makeQuery(id+"F0.imprint","IMPRINT",FACE,{"disambiguationData":[TD([[makeQuery(id+"F0.imprint","IMPRINT",EDGE,{"disambiguationData":[TD([[subQ2,1.0]])],"derivedFrom":subQ1}),1.0]])]});}
            var Q10;
            {var subQ3=sQuery(id+"F0.wireOp",EDGE,"QIJiGY5w-lFCi-xx9X-rp0q-5GBFziIUs7mU");var subQ5=sQuery(id+"F0.wireOp",EDGE,"E19");var subQ6=makeQuery(id+"F0.imprint","INTERSECT",VERTEX,{"disambiguationData":[OD(1.0)],"derivedFrom":[subQ3,subQ5]});Q10=makeQuery(id+"F0.imprint","IMPRINT",FACE,{"disambiguationData":[TD([[makeQuery(id+"F0.imprint","IMPRINT",EDGE,{"disambiguationData":[TD([[subQ6,-1.0]])],"derivedFrom":subQ5}),-1.0]])]});}
            var Q11;
            {var subQ0=sQuery(id+"F0.wireOp",EDGE,"E19");var subQ6=sQuery(id+"F0.wireOp",EDGE,"QIJiGY5w-lFCi-xx9X-rp0q-5GBFziIUs7mU");var subQ8=makeQuery(id+"F0.imprint","INTERSECT",VERTEX,{"disambiguationData":[OD(0.0)],"derivedFrom":[subQ6,subQ0]});Q11=makeQuery(id+"F0.imprint","IMPRINT",FACE,{"disambiguationData":[TD([[makeQuery(id+"F0.imprint","IMPRINT",EDGE,{"disambiguationData":[TD([[subQ8,1.0]])],"derivedFrom":subQ0}),-1.0]])]});}
            var Q12;
            {var subQ0=sQuery(id+"F0.wireOp",EDGE,"QIJiGY5w-lFCi-xx9X-rp0q-5GBFziIUs7mU");var subQ5=sQuery(id+"F0.wireOp",EDGE,"E19");var subQ6=makeQuery(id+"F0.imprint","INTERSECT",VERTEX,{"disambiguationData":[OD(0.0)],"derivedFrom":[subQ0,subQ5]});Q12=makeQuery(id+"F0.imprint","IMPRINT",FACE,{"disambiguationData":[TD([[makeQuery(id+"F0.imprint","IMPRINT",EDGE,{"disambiguationData":[TD([[subQ6,-1.0]])],"derivedFrom":subQ5}),-1.0]])]});}
            var Q13;
            {var subQ0=sQuery(id+"F0.wireOp",EDGE,"E19");var subQ6=sQuery(id+"F0.wireOp",EDGE,"QIJiGY5w-lFCi-xx9X-rp0q-5GBFziIUs7mU");var subQ8=makeQuery(id+"F0.imprint","INTERSECT",VERTEX,{"disambiguationData":[OD(1.0)],"derivedFrom":[subQ6,subQ0]});Q13=makeQuery(id+"F0.imprint","IMPRINT",FACE,{"disambiguationData":[TD([[makeQuery(id+"F0.imprint","IMPRINT",EDGE,{"disambiguationData":[TD([[subQ8,1.0]])],"derivedFrom":subQ0}),-1.0]])]});}
            var Q14;
            {var subQ0=sQuery(id+"F0.wireOp",EDGE,"E16");var subQ4=sQuery(id+"F0.wireOp",EDGE,"E5");var subQ5=makeQuery(id+"F0.imprint","INTERSECT",VERTEX,{"disambiguationData":[OD(1.0)],"derivedFrom":[subQ4,subQ0]});Q14=makeQuery(id+"F0.imprint","IMPRINT",FACE,{"disambiguationData":[TD([[makeQuery(id+"F0.imprint","IMPRINT",EDGE,{"disambiguationData":[TD([[subQ5,1.0]])],"derivedFrom":subQ4}),1.0]])]});}
            var Q15;
            {var subQ0=sQuery(id+"F0.wireOp",EDGE,"E16");var subQ1=sQuery(id+"F0.wireOp",EDGE,"QIJiGY5w-lFCi-xx9X-rp0q-5GBFziIUs7mU");var subQ2=makeQuery(id+"F0.imprint","INTERSECT",VERTEX,{"derivedFrom":[subQ1,subQ0]});Q15=makeQuery(id+"F0.imprint","IMPRINT",FACE,{"disambiguationData":[TD([[makeQuery(id+"F0.imprint","IMPRINT",EDGE,{"disambiguationData":[TD([[subQ2,1.0]])],"derivedFrom":subQ1}),1.0]])]});}
            var Q16;
            {var subQ0=sQuery(id+"F0.wireOp",EDGE,"E16");var subQ1=sQuery(id+"F0.wireOp",EDGE,"QIJiGY5w-lFCi-xx9X-rp0q-5GBFziIUs7mU");var subQ2=makeQuery(id+"F0.imprint","INTERSECT",VERTEX,{"derivedFrom":[subQ1,subQ0]});Q16=makeQuery(id+"F0.imprint","IMPRINT",FACE,{"disambiguationData":[TD([[makeQuery(id+"F0.imprint","IMPRINT",EDGE,{"disambiguationData":[TD([[subQ2,1.0]])],"derivedFrom":subQ1}),-1.0]])]});}
            var Q17;
            {var subQ0=sQuery(id+"F0.wireOp",EDGE,"E16");var subQ4=sQuery(id+"F0.wireOp",EDGE,"E5");var subQ5=makeQuery(id+"F0.imprint","INTERSECT",VERTEX,{"disambiguationData":[OD(0.0)],"derivedFrom":[subQ4,subQ0]});Q17=makeQuery(id+"F0.imprint","IMPRINT",FACE,{"disambiguationData":[TD([[makeQuery(id+"F0.imprint","IMPRINT",EDGE,{"disambiguationData":[TD([[subQ5,-1.0]])],"derivedFrom":subQ4}),1.0]])]});}
            var Q18;
            {var subQ0=sQuery(id+"F0.wireOp",EDGE,"E15");var subQ1=sQuery(id+"F0.wireOp",EDGE,"E5");var subQ2=makeQuery(id+"F0.imprint","INTERSECT",VERTEX,{"disambiguationData":[OD(0.0)],"derivedFrom":[subQ1,subQ0]});Q18=makeQuery(id+"F0.imprint","IMPRINT",FACE,{"disambiguationData":[TD([[makeQuery(id+"F0.imprint","IMPRINT",EDGE,{"disambiguationData":[TD([[subQ2,-1.0]])],"derivedFrom":subQ1}),-1.0]])]});}
            var Q19;
            {var subQ0=sQuery(id+"F0.wireOp",EDGE,"E15");var subQ4=sQuery(id+"F0.wireOp",EDGE,"E5");var subQ8=makeQuery(id+"F0.imprint","INTERSECT",VERTEX,{"disambiguationData":[OD(0.0)],"derivedFrom":[subQ4,subQ0]});Q19=makeQuery(id+"F0.imprint","IMPRINT",FACE,{"disambiguationData":[TD([[makeQuery(id+"F0.imprint","IMPRINT",EDGE,{"disambiguationData":[TD([[subQ8,-1.0]])],"derivedFrom":subQ4}),1.0]])]});}
            var Q20;
            {var subQ0=sQuery(id+"F0.wireOp",EDGE,"E14");var subQ4=sQuery(id+"F0.wireOp",EDGE,"E5");var subQ5=makeQuery(id+"F0.imprint","INTERSECT",VERTEX,{"disambiguationData":[OD(1.0)],"derivedFrom":[subQ4,subQ0]});Q20=makeQuery(id+"F0.imprint","IMPRINT",FACE,{"disambiguationData":[TD([[makeQuery(id+"F0.imprint","IMPRINT",EDGE,{"disambiguationData":[TD([[subQ5,1.0]])],"derivedFrom":subQ4}),1.0]])]});}
            var Q21;
            {var subQ0=sQuery(id+"F0.wireOp",EDGE,"E14");var subQ1=sQuery(id+"F0.wireOp",EDGE,"b7w3sZkz-h2S3-PTXa-qy05-PL4N3AHQH3GV");var subQ2=makeQuery(id+"F0.imprint","INTERSECT",VERTEX,{"derivedFrom":[subQ1,subQ0]});Q21=makeQuery(id+"F0.imprint","IMPRINT",FACE,{"disambiguationData":[TD([[makeQuery(id+"F0.imprint","IMPRINT",EDGE,{"disambiguationData":[TD([[subQ2,1.0]])],"derivedFrom":subQ1}),1.0]])]});}
            var Q22;
            {var subQ0=sQuery(id+"F0.wireOp",EDGE,"E14");var subQ1=sQuery(id+"F0.wireOp",EDGE,"b7w3sZkz-h2S3-PTXa-qy05-PL4N3AHQH3GV");var subQ2=makeQuery(id+"F0.imprint","INTERSECT",VERTEX,{"derivedFrom":[subQ1,subQ0]});Q22=makeQuery(id+"F0.imprint","IMPRINT",FACE,{"disambiguationData":[TD([[makeQuery(id+"F0.imprint","IMPRINT",EDGE,{"disambiguationData":[TD([[subQ2,1.0]])],"derivedFrom":subQ1}),-1.0]])]});}
            var Q23;
            {var subQ0=sQuery(id+"F0.wireOp",EDGE,"E14");var subQ6=sQuery(id+"F0.wireOp",EDGE,"E5");var subQ7=makeQuery(id+"F0.imprint","INTERSECT",VERTEX,{"disambiguationData":[OD(0.0)],"derivedFrom":[subQ6,subQ0]});Q23=makeQuery(id+"F0.imprint","IMPRINT",FACE,{"disambiguationData":[TD([[makeQuery(id+"F0.imprint","IMPRINT",EDGE,{"disambiguationData":[TD([[subQ7,-1.0]])],"derivedFrom":subQ6}),1.0]])]});}
            extrude(context, id + "F4", {"entities" : qUnion([Q0, Q1, Q2, Q3, Q4, Q5, Q6, Q7, Q8, Q9, Q10, Q11, Q12, Q13, Q14, Q15, Q16, Q17, Q18, Q19, Q20, Q21, Q22, Q23]), "operationType" : NewBodyOperationType.ADD, "depth" : 3 * mm, "offsetDistance" : 25 * mm});
        }
        {
            var Q0;
            {var subQ0=sQuery(id+"F1.wireOp",EDGE,"E52");Q0=makeQuery(id+"F1.imprint","IMPRINT",FACE,{"disambiguationData":[TD([[makeQuery(id+"F1.imprint","IMPRINT",EDGE,{"derivedFrom":subQ0}),1.0]])]});}
            var Q1;
            {var subQ0=sQuery(id+"F1.wireOp",EDGE,"E108");Q1=makeQuery(id+"F1.imprint","IMPRINT",FACE,{"disambiguationData":[TD([[makeQuery(id+"F1.imprint","IMPRINT",EDGE,{"derivedFrom":subQ0}),1.0]])]});}
            var Q2;
            {var subQ0=sQuery(id+"F1.wireOp",EDGE,"E90");Q2=makeQuery(id+"F1.imprint","IMPRINT",FACE,{"disambiguationData":[TD([[makeQuery(id+"F1.imprint","IMPRINT",EDGE,{"derivedFrom":subQ0}),1.0]])]});}
            var Q3;
            {var subQ0=sQuery(id+"F1.wireOp",EDGE,"E58");Q3=makeQuery(id+"F1.imprint","IMPRINT",FACE,{"disambiguationData":[TD([[makeQuery(id+"F1.imprint","IMPRINT",EDGE,{"derivedFrom":subQ0}),-1.0]])]});}
            var Q4;
            {var subQ0=sQuery(id+"F1.wireOp",EDGE,"E62");var subQ1=sQuery(id+"F1.wireOp",EDGE,"E55");var subQ2=makeQuery(id+"F1.imprint","INTERSECT",VERTEX,{"derivedFrom":[subQ1,subQ0]});Q4=makeQuery(id+"F1.imprint","IMPRINT",FACE,{"disambiguationData":[TD([[makeQuery(id+"F1.imprint","IMPRINT",EDGE,{"disambiguationData":[TD([[subQ2,1.0]])],"derivedFrom":subQ1}),1.0]])]});}
            var Q5;
            {var subQ0=sQuery(id+"F1.wireOp",EDGE,"E57");Q5=makeQuery(id+"F1.imprint","IMPRINT",FACE,{"disambiguationData":[TD([[makeQuery(id+"F1.imprint","IMPRINT",EDGE,{"derivedFrom":subQ0}),1.0]])]});}
            var Q6;
            {var subQ0=sQuery(id+"F1.wireOp",EDGE,"E61");var subQ1=sQuery(id+"F1.wireOp",EDGE,"E55");var subQ2=makeQuery(id+"F1.imprint","INTERSECT",VERTEX,{"derivedFrom":[subQ1,subQ0]});Q6=makeQuery(id+"F1.imprint","IMPRINT",FACE,{"disambiguationData":[TD([[makeQuery(id+"F1.imprint","IMPRINT",EDGE,{"disambiguationData":[TD([[subQ2,-1.0]])],"derivedFrom":subQ1}),1.0]])]});}
            var Q7;
            {var subQ4=sQuery(id+"F1.wireOp",EDGE,"E53");Q7=makeQuery(id+"F1.imprint","IMPRINT",FACE,{"disambiguationData":[TD([[makeQuery(id+"F1.imprint","IMPRINT",EDGE,{"derivedFrom":subQ4}),1.0]])]});}
            extrude(context, id + "F5", {"entities" : qUnion([Q0, Q1, Q2, Q3, Q4, Q5, Q6, Q7]), "operationType" : NewBodyOperationType.ADD, "depth" : 3 * mm, "offsetDistance" : 25 * mm});
        }
        {
            var Q0;
            {var subQ3=sQuery(id+"F1.wireOp",EDGE,"ej4slr3Q-Yw2a-d8uW-XIuV-5FMGxbp2aJ1O");var subQ5=sQuery(id+"F1.wireOp",EDGE,"E74");var subQ7=makeQuery(id+"F1.imprint","INTERSECT",VERTEX,{"derivedFrom":[subQ5,subQ3]});Q0=makeQuery(id+"F1.imprint","IMPRINT",FACE,{"disambiguationData":[TD([[makeQuery(id+"F1.imprint","IMPRINT",EDGE,{"disambiguationData":[TD([[subQ7,-1.0]])],"derivedFrom":subQ5}),-1.0]])]});}
            extrude(context, id + "F6", {"entities" : qUnion([Q0]), "depth" : 3 * mm, "offsetDistance" : 25 * mm});
        }
        {
            var Q0;
            {var subQ0=sQuery(id+"F1.wireOp",EDGE,"E53");Q0=makeQuery(id+"F1.imprint","IMPRINT",FACE,{"disambiguationData":[TD([[makeQuery(id+"F1.imprint","IMPRINT",EDGE,{"derivedFrom":subQ0}),1.0]])]});}
            var sketch = newSketch(context, id + "F7", { "sketchPlane" : qUnion([Q0])});
            skPoint(sketch, "E651.0", {"position": v(-57.5, -67.99) * mm});
            skPoint(sketch, "E651.1", {"position": v(57.5, -67.99) * mm});
            skLineSegment(sketch, "E652.top", {"start": v(57.5, -123.98) * mm, "end": v(-57.5, -123.98) * mm});
            skLineSegment(sketch, "E652.left", {"start": v(57.5, -67.99) * mm, "end": v(57.5, -123.98) * mm});
            skLineSegment(sketch, "E652.right", {"start": v(-57.5, -67.98) * mm, "end": v(-57.5, -123.98) * mm});
            skPoint(sketch, "E653", {"position": v(-52.48, -71.6) * mm});
            skPoint(sketch, "E654", {"position": v(-52.45, -118.6) * mm});
            skPoint(sketch, "E655", {"position": v(-52.48, -106.35) * mm});
            skPoint(sketch, "E656", {"position": v(-52.54, -108.35) * mm});
            skPoint(sketch, "E657", {"position": v(-52.5, -81.85) * mm});
            skPoint(sketch, "E658", {"position": v(-52.5, -83.85) * mm});
            skPoint(sketch, "E659", {"position": v(-52.45, -94.1) * mm});
            skPoint(sketch, "E660", {"position": v(-52.48, -96.1) * mm});
            skPoint(sketch, "E661", {"position": v(-43.25, -67.98) * mm});
            skPoint(sketch, "E662", {"position": v(-34, -67.98) * mm});
            skPoint(sketch, "E663", {"position": v(-29.36, -67.98) * mm});
            skPoint(sketch, "E664", {"position": v(-24.73, -67.98) * mm});
            skPoint(sketch, "E665", {"position": v(-38.63, -67.98) * mm});
            skPoint(sketch, "E666", {"position": v(24.63, -67.98) * mm});
            skPoint(sketch, "E667", {"position": v(29.26, -67.98) * mm});
            skPoint(sketch, "E668", {"position": v(33.89, -67.98) * mm});
            skPoint(sketch, "E669", {"position": v(38.52, -67.98) * mm});
            skPoint(sketch, "E670", {"position": v(43.15, -67.99) * mm});
            skPoint(sketch, "E671", {"position": v(-8, -67.98) * mm});
            skPoint(sketch, "E672", {"position": v(-5.35, -67.98) * mm});
            skPoint(sketch, "E673", {"position": v(-2.72, -67.98) * mm});
            skPoint(sketch, "E674", {"position": v(0.01, -67.98) * mm});
            skPoint(sketch, "E675", {"position": v(2.57, -67.98) * mm});
            skPoint(sketch, "E676", {"position": v(5.25, -67.98) * mm});
            skPoint(sketch, "E677", {"position": v(7.82, -67.98) * mm});
            skArc(sketch, "E678", {"start": v(-8, -67.98) * mm, "mid": v(0.01, -75.99) * mm, "end": v(8.02, -67.98) * mm});
            skArc(sketch, "E679", {"start": v(-5.35, -67.98) * mm, "mid": v(-0.76, -73.29) * mm, "end": v(5.16, -69.5) * mm});
            skArc(sketch, "E680", {"start": v(-2.72, -67.98) * mm, "mid": v(-0.54, -70.66) * mm, "end": v(2.53, -69.05) * mm});
            skArc(sketch, "E681", {"start": v(-10.45, -67.98) * mm, "mid": v(0.01, -78.44) * mm, "end": v(10.47, -67.98) * mm});
            skArc(sketch, "E682", {"start": v(-8, -67.98) * mm, "mid": v(0.95, -60.02) * mm, "end": v(7.8, -69.85) * mm});
            skArc(sketch, "E683", {"start": v(-5.35, -67.98) * mm, "mid": v(0.78, -62.66) * mm, "end": v(5.16, -69.5) * mm});
            skArc(sketch, "E684", {"start": v(-2.72, -67.98) * mm, "mid": v(0.56, -65.3) * mm, "end": v(2.53, -69.05) * mm});
            skPoint(sketch, "E685", {"position": v(-36.31, -67.98) * mm});
            skArc(sketch, "E686", {"start": v(-36.31, -67.98) * mm, "mid": v(-34, -65.66) * mm, "end": v(-31.69, -67.98) * mm});
            skArc(sketch, "E687", {"start": v(-38.63, -67.98) * mm, "mid": v(-34, -63.35) * mm, "end": v(-29.37, -67.98) * mm});
            skLineSegment(sketch, "E688", {"start": v(-34, -67.98) * mm, "end": v(-34, -67.98) * mm});
            skArc(sketch, "E689", {"start": v(15.3, -67.98) * mm, "mid": v(33.89, -49.4) * mm, "end": v(52.46, -67.98) * mm});
            skArc(sketch, "E690", {"start": v(24.63, -67.98) * mm, "mid": v(33.89, -58.72) * mm, "end": v(43.15, -67.98) * mm});
            skArc(sketch, "E691", {"start": v(29.26, -67.98) * mm, "mid": v(33.89, -63.35) * mm, "end": v(38.52, -67.98) * mm});
            skArc(sketch, "E692", {"start": v(31.57, -67.98) * mm, "mid": v(33.89, -65.67) * mm, "end": v(36.2, -67.98) * mm});
            skPoint(sketch, "E693", {"position": v(-47.87, -71.6) * mm});
            skPoint(sketch, "E694", {"position": v(-47.87, -67.98) * mm});
            skPoint(sketch, "E695", {"position": v(-43.24, -71.6) * mm});
            skPoint(sketch, "E696", {"position": v(-38.66, -71.6) * mm});
            skPoint(sketch, "E697", {"position": v(-36.32, -71.6) * mm});
            skPoint(sketch, "E698", {"position": v(-33.97, -71.6) * mm});
            skPoint(sketch, "E699", {"position": v(-31.68, -71.6) * mm});
            skPoint(sketch, "E700", {"position": v(-29.37, -71.6) * mm});
            skPoint(sketch, "E701", {"position": v(-24.77, -71.6) * mm});
            skLineSegment(sketch, "E702.top", {"start": v(-43.26, -71.6) * mm, "end": v(-38.66, -71.6) * mm});
            skLineSegment(sketch, "E703.top", {"start": v(-29.37, -71.6) * mm, "end": v(-24.77, -71.6) * mm});
            skPoint(sketch, "E704", {"position": v(-43.23, -81.85) * mm});
            skPoint(sketch, "E705", {"position": v(-38.62, -81.85) * mm});
            skPoint(sketch, "E706", {"position": v(-36.3, -81.85) * mm});
            skPoint(sketch, "E707", {"position": v(-34, -81.85) * mm});
            skPoint(sketch, "E708", {"position": v(-31.67, -81.85) * mm});
            skPoint(sketch, "E709", {"position": v(-29.36, -81.85) * mm});
            skPoint(sketch, "E710", {"position": v(-43.18, -83.85) * mm});
            skPoint(sketch, "E711", {"position": v(-38.64, -83.85) * mm});
            skPoint(sketch, "E712", {"position": v(-36.32, -83.85) * mm});
            skPoint(sketch, "E713", {"position": v(-34, -83.85) * mm});
            skPoint(sketch, "E714", {"position": v(-31.68, -83.85) * mm});
            skPoint(sketch, "E715", {"position": v(-29.37, -83.85) * mm});
            skPoint(sketch, "E716", {"position": v(-47.9, -81.85) * mm});
            skPoint(sketch, "E717", {"position": v(-47.87, -83.85) * mm});
            skLineSegment(sketch, "E718", {"start": v(-52.5, -81.85) * mm, "end": v(-47.9, -81.85) * mm});
            skLineSegment(sketch, "E719", {"start": v(-47.87, -83.85) * mm, "end": v(-52.5, -83.85) * mm});
            skPoint(sketch, "E720", {"position": v(-47.91, -94.1) * mm});
            skPoint(sketch, "E721", {"position": v(-47.88, -96.1) * mm});
            skPoint(sketch, "E722", {"position": v(-43.2, -94.1) * mm});
            skPoint(sketch, "E723", {"position": v(-43.2, -96.1) * mm});
            skPoint(sketch, "E724", {"position": v(-38.61, -94.1) * mm});
            skPoint(sketch, "E725", {"position": v(-36.31, -94.1) * mm});
            skPoint(sketch, "E726", {"position": v(-34.02, -94.1) * mm});
            skPoint(sketch, "E727", {"position": v(-31.68, -94.1) * mm});
            skPoint(sketch, "E728", {"position": v(-29.38, -94.1) * mm});
            skPoint(sketch, "E729", {"position": v(-24.75, -94.1) * mm});
            skPoint(sketch, "E730", {"position": v(-38.61, -96.1) * mm});
            skPoint(sketch, "E731", {"position": v(-36.31, -96.1) * mm});
            skPoint(sketch, "E732", {"position": v(-34.02, -96.1) * mm});
            skPoint(sketch, "E733", {"position": v(-31.68, -96.1) * mm});
            skPoint(sketch, "E734", {"position": v(-29.38, -96.1) * mm});
            skPoint(sketch, "E735", {"position": v(-24.75, -96.1) * mm});
            skPoint(sketch, "E736", {"position": v(-47.98, -106.35) * mm});
            skPoint(sketch, "E737", {"position": v(-43.2, -106.35) * mm});
            skPoint(sketch, "E738", {"position": v(-38.66, -106.35) * mm});
            skPoint(sketch, "E739", {"position": v(-36.36, -106.35) * mm});
            skPoint(sketch, "E740", {"position": v(-34.06, -106.35) * mm});
            skPoint(sketch, "E741", {"position": v(-31.68, -106.35) * mm});
            skPoint(sketch, "E742", {"position": v(-29.4, -106.35) * mm});
            skPoint(sketch, "E743", {"position": v(-24.74, -106.35) * mm});
            skPoint(sketch, "E744", {"position": v(-47.98, -108.35) * mm});
            skPoint(sketch, "E745", {"position": v(-43.2, -108.35) * mm});
            skPoint(sketch, "E746", {"position": v(-38.72, -108.35) * mm});
            skPoint(sketch, "E747", {"position": v(-36.33, -108.35) * mm});
            skPoint(sketch, "E748", {"position": v(-34.06, -108.35) * mm});
            skPoint(sketch, "E749", {"position": v(-31.68, -108.35) * mm});
            skPoint(sketch, "E750", {"position": v(-29.4, -108.35) * mm});
            skPoint(sketch, "E751", {"position": v(-24.74, -108.35) * mm});
            skPoint(sketch, "E752", {"position": v(-47.92, -118.6) * mm});
            skPoint(sketch, "E753", {"position": v(-43.2, -118.6) * mm});
            skPoint(sketch, "E754", {"position": v(-38.72, -118.6) * mm});
            skPoint(sketch, "E755", {"position": v(-36.33, -118.6) * mm});
            skPoint(sketch, "E756", {"position": v(-34.06, -118.6) * mm});
            skPoint(sketch, "E757", {"position": v(-31.68, -118.6) * mm});
            skPoint(sketch, "E758", {"position": v(-29.4, -118.6) * mm});
            skPoint(sketch, "E759", {"position": v(-24.74, -118.6) * mm});
            skLineSegment(sketch, "E760", {"start": v(-52.54, -108.35) * mm, "end": v(-47.98, -108.35) * mm});
            skLineSegment(sketch, "E761", {"start": v(-47.92, -118.6) * mm, "end": v(-52.45, -118.6) * mm});
            skLineSegment(sketch, "E762", {"start": v(-43.2, -108.35) * mm, "end": v(-38.72, -108.35) * mm});
            skLineSegment(sketch, "E763", {"start": v(-38.72, -118.6) * mm, "end": v(-43.2, -118.6) * mm});
            skLineSegment(sketch, "E764", {"start": v(-47.87, -71.6) * mm, "end": v(-52.48, -71.6) * mm});
            skLineSegment(sketch, "E765.top", {"start": v(-52.5, -71.6) * mm, "end": v(-47.87, -71.6) * mm});
            skLineSegment(sketch, "E766.bottom", {"start": v(-52.5, -81.85) * mm, "end": v(-47.87, -81.85) * mm});
            skLineSegment(sketch, "E766.top", {"start": v(-52.5, -83.85) * mm, "end": v(-47.87, -83.85) * mm});
            skLineSegment(sketch, "E767.left", {"start": v(-38.66, -71.6) * mm, "end": v(-38.66, -81.85) * mm});
            skLineSegment(sketch, "E768.left", {"start": v(-38.64, -83.85) * mm, "end": v(-38.64, -94.1) * mm});
            skLineSegment(sketch, "E768.right", {"start": v(-36.31, -83.85) * mm, "end": v(-36.31, -94.1) * mm});
            skLineSegment(sketch, "E769.bottom", {"start": v(-52.45, -94.1) * mm, "end": v(-47.88, -94.1) * mm});
            skLineSegment(sketch, "E769.top", {"start": v(-52.5, -96.1) * mm, "end": v(-47.88, -96.1) * mm});
            skLineSegment(sketch, "E770.bottom", {"start": v(-52.48, -106.35) * mm, "end": v(-47.98, -106.35) * mm});
            skLineSegment(sketch, "E770.top", {"start": v(-52.48, -108.35) * mm, "end": v(-47.98, -108.35) * mm});
            skLineSegment(sketch, "E771.top", {"start": v(-52.45, -123.98) * mm, "end": v(-24.8, -123.98) * mm});
            skLineSegment(sketch, "E772.left", {"start": v(-38.61, -96.1) * mm, "end": v(-38.66, -106.35) * mm});
            skLineSegment(sketch, "E772.right", {"start": v(-36.31, -96.1) * mm, "end": v(-36.36, -106.35) * mm});
            skLineSegment(sketch, "E773", {"start": v(-38.72, -108.35) * mm, "end": v(-38.72, -118.6) * mm});
            skLineSegment(sketch, "E774", {"start": v(-36.33, -118.6) * mm, "end": v(-36.33, -108.35) * mm});
            skLineSegment(sketch, "E775", {"start": v(-29.37, -71.6) * mm, "end": v(-29.36, -81.85) * mm});
            skLineSegment(sketch, "E776", {"start": v(-29.37, -83.85) * mm, "end": v(-29.38, -94.1) * mm});
            skLineSegment(sketch, "E777", {"start": v(-29.38, -96.1) * mm, "end": v(-29.4, -106.35) * mm});
            skLineSegment(sketch, "E778", {"start": v(-29.4, -108.35) * mm, "end": v(-29.4, -118.6) * mm});
            skLineSegment(sketch, "E779", {"start": v(-43.18, -83.85) * mm, "end": v(-38.64, -83.85) * mm});
            skLineSegment(sketch, "E780", {"start": v(-43.23, -81.85) * mm, "end": v(-38.66, -81.85) * mm});
            skPoint(sketch, "E781", {"position": v(-24.74, -81.82) * mm});
            skLineSegment(sketch, "E782", {"start": v(-29.37, -83.85) * mm, "end": v(-24.74, -83.86) * mm});
            skLineSegment(sketch, "E783", {"start": v(-36.31, -83.85) * mm, "end": v(-31.68, -83.85) * mm});
            skLineSegment(sketch, "E784", {"start": v(-36.3, -81.85) * mm, "end": v(-31.67, -81.85) * mm});
            skLineSegment(sketch, "E785", {"start": v(-31.68, -83.85) * mm, "end": v(-31.68, -94.1) * mm});
            skLineSegment(sketch, "E786", {"start": v(-29.36, -81.85) * mm, "end": v(-24.74, -81.82) * mm});
            skLineSegment(sketch, "E787", {"start": v(-52.48, -71.6) * mm, "end": v(-52.5, -81.85) * mm});
            skLineSegment(sketch, "E788", {"start": v(-47.98, -108.35) * mm, "end": v(-47.92, -118.6) * mm});
            skLineSegment(sketch, "E789", {"start": v(-31.68, -108.35) * mm, "end": v(-31.68, -118.6) * mm});
            skLineSegment(sketch, "E790", {"start": v(-31.68, -96.1) * mm, "end": v(-31.68, -106.35) * mm});
            skLineSegment(sketch, "E791", {"start": v(-29.4, -118.6) * mm, "end": v(-24.8, -118.6) * mm});
            skLineSegment(sketch, "E792", {"start": v(-36.33, -118.6) * mm, "end": v(-31.68, -118.6) * mm});
            skPoint(sketch, "E793", {"position": v(-20.11, -94.1) * mm});
            skPoint(sketch, "E794", {"position": v(-15.49, -94.1) * mm});
            skPoint(sketch, "E795", {"position": v(-20.11, -96.1) * mm});
            skPoint(sketch, "E796", {"position": v(-15.49, -96.1) * mm});
            skLineSegment(sketch, "E797", {"start": v(-29.38, -94.1) * mm, "end": v(-24.75, -94.1) * mm});
            skLineSegment(sketch, "E798", {"start": v(-20.11, -94.1) * mm, "end": v(-15.49, -94.1) * mm});
            skLineSegment(sketch, "E799", {"start": v(-29.38, -96.1) * mm, "end": v(-24.75, -96.1) * mm});
            skLineSegment(sketch, "E800", {"start": v(-20.11, -96.1) * mm, "end": v(-15.49, -96.1) * mm});
            skLineSegment(sketch, "E801", {"start": v(-43.2, -94.1) * mm, "end": v(-38.64, -94.1) * mm});
            skLineSegment(sketch, "E802", {"start": v(-43.2, -96.1) * mm, "end": v(-38.61, -96.1) * mm});
            skLineSegment(sketch, "E803", {"start": v(-36.31, -94.1) * mm, "end": v(-31.68, -94.1) * mm});
            skLineSegment(sketch, "E804", {"start": v(-36.31, -96.1) * mm, "end": v(-31.68, -96.1) * mm});
            skPoint(sketch, "E805", {"position": v(-20.1, -106.35) * mm});
            skPoint(sketch, "E806", {"position": v(-20.1, -108.35) * mm});
            skPoint(sketch, "E807", {"position": v(-15.52, -106.35) * mm});
            skPoint(sketch, "E808", {"position": v(-15.52, -108.35) * mm});
            skLineSegment(sketch, "E809", {"start": v(-29.4, -106.35) * mm, "end": v(-24.74, -106.35) * mm});
            skLineSegment(sketch, "E810", {"start": v(-20.1, -106.35) * mm, "end": v(-15.52, -106.35) * mm});
            skLineSegment(sketch, "E811", {"start": v(-29.4, -108.35) * mm, "end": v(-24.74, -108.35) * mm});
            skLineSegment(sketch, "E812", {"start": v(-36.33, -108.35) * mm, "end": v(-31.68, -108.35) * mm});
            skLineSegment(sketch, "E813", {"start": v(-36.36, -106.35) * mm, "end": v(-31.68, -106.35) * mm});
            skLineSegment(sketch, "E814", {"start": v(-43.2, -106.35) * mm, "end": v(-38.66, -106.35) * mm});
            skLineSegment(sketch, "E815", {"start": v(-20.1, -108.35) * mm, "end": v(-15.52, -108.35) * mm});
            skLineSegment(sketch, "E816", {"start": v(-20.05, -118.53) * mm, "end": v(-15.5, -118.53) * mm});
            skPoint(sketch, "E817", {"position": v(-20.08, -81.8) * mm});
            skPoint(sketch, "E818", {"position": v(-20.08, -83.8) * mm});
            skPoint(sketch, "E819", {"position": v(-15.53, -81.8) * mm});
            skPoint(sketch, "E820", {"position": v(-15.53, -83.8) * mm});
            skLineSegment(sketch, "E821", {"start": v(-20.08, -81.8) * mm, "end": v(-15.53, -81.8) * mm});
            skLineSegment(sketch, "E822", {"start": v(-20.08, -83.8) * mm, "end": v(-15.53, -83.8) * mm});
            skLineSegment(sketch, "E823", {"start": v(-36.3, -71.6) * mm, "end": v(-31.68, -71.6) * mm});
            skLineSegment(sketch, "E824", {"start": v(-43.24, -71.6) * mm, "end": v(-38.66, -71.6) * mm});
            skLineSegment(sketch, "E825", {"start": v(-36.3, -71.6) * mm, "end": v(-36.3, -81.85) * mm});
            skLineSegment(sketch, "E826", {"start": v(-36.31, -67.98) * mm, "end": v(-36.31, -69.55) * mm});
            skLineSegment(sketch, "E827", {"start": v(-24.74, -118.6) * mm, "end": v(-15.5, -118.53) * mm});
            skLineSegment(sketch, "E828", {"start": v(-29.4, -118.6) * mm, "end": v(-24.74, -118.6) * mm});
            skLineSegment(sketch, "E829", {"start": v(-31.69, -67.98) * mm, "end": v(-31.68, -69.55) * mm});
            skLineSegment(sketch, "E830", {"start": v(-31.68, -71.6) * mm, "end": v(-31.67, -81.85) * mm});
            skPoint(sketch, "E831", {"position": v(-26.93, -50.9) * mm});
            skLineSegment(sketch, "E832", {"start": v(-50.57, -59.32) * mm, "end": v(-50.6, -59.3) * mm});
            skLineSegment(sketch, "E833", {"start": v(-34, -49.49) * mm, "end": v(-34, -67.98) * mm});
            skLineSegment(sketch, "E834", {"start": v(-41.1, -50.84) * mm, "end": v(-34, -67.98) * mm});
            skLineSegment(sketch, "E835", {"start": v(-26.93, -50.9) * mm, "end": v(-34, -67.98) * mm});
            skPoint(sketch, "E836", {"position": v(-51.12, -60.89) * mm});
            skLineSegment(sketch, "E837", {"start": v(-20.92, -54.9) * mm, "end": v(-34, -67.98) * mm});
            skPoint(sketch, "E838", {"position": v(-20.09, -67.93) * mm});
            skLineSegment(sketch, "E839", {"start": v(-47.06, -54.91) * mm, "end": v(-34, -67.98) * mm});
            skLineSegment(sketch, "E840", {"start": v(-52.5, -83.85) * mm, "end": v(-52.45, -94.1) * mm});
            skLineSegment(sketch, "E841", {"start": v(-47.87, -83.85) * mm, "end": v(-47.88, -94.1) * mm});
            skLineSegment(sketch, "E842", {"start": v(-43.18, -83.85) * mm, "end": v(-43.2, -94.1) * mm});
            skLineSegment(sketch, "E843", {"start": v(-52.5, -96.1) * mm, "end": v(-52.48, -106.35) * mm});
            skLineSegment(sketch, "E844", {"start": v(-47.88, -96.1) * mm, "end": v(-47.98, -106.35) * mm});
            skLineSegment(sketch, "E845", {"start": v(-43.2, -96.1) * mm, "end": v(-43.2, -106.35) * mm});
            skLineSegment(sketch, "E846", {"start": v(-52.48, -108.35) * mm, "end": v(-52.45, -118.6) * mm});
            skLineSegment(sketch, "E847", {"start": v(-43.2, -108.35) * mm, "end": v(-43.2, -118.6) * mm});
            skLineSegment(sketch, "E848", {"start": v(-24.74, -108.35) * mm, "end": v(-24.74, -118.6) * mm});
            skLineSegment(sketch, "E849", {"start": v(-24.75, -96.1) * mm, "end": v(-24.74, -106.35) * mm});
            skLineSegment(sketch, "E850", {"start": v(-20.1, -108.35) * mm, "end": v(-20.05, -118.53) * mm});
            skLineSegment(sketch, "E851", {"start": v(-15.52, -108.35) * mm, "end": v(-15.5, -118.53) * mm});
            skLineSegment(sketch, "E852", {"start": v(-20.11, -96.1) * mm, "end": v(-20.1, -106.35) * mm});
            skLineSegment(sketch, "E853", {"start": v(-15.49, -96.1) * mm, "end": v(-15.52, -106.35) * mm});
            skLineSegment(sketch, "E854", {"start": v(-24.74, -83.86) * mm, "end": v(-24.75, -94.1) * mm});
            skLineSegment(sketch, "E855", {"start": v(-20.08, -83.8) * mm, "end": v(-20.11, -94.1) * mm});
            skLineSegment(sketch, "E856", {"start": v(-15.53, -83.8) * mm, "end": v(-15.49, -94.1) * mm});
            skLineSegment(sketch, "E857", {"start": v(-24.77, -71.6) * mm, "end": v(-24.74, -81.82) * mm});
            skLineSegment(sketch, "E858", {"start": v(-43.24, -71.6) * mm, "end": v(-43.23, -81.85) * mm});
            skLineSegment(sketch, "E859", {"start": v(-47.87, -71.6) * mm, "end": v(-47.87, -81.85) * mm});
            skLineSegment(sketch, "E860", {"start": v(-52.52, -67.95) * mm, "end": v(-15.48, -67.95) * mm});
            skLineSegment(sketch, "E861", {"start": v(-36.31, -69.55) * mm, "end": v(-31.68, -69.55) * mm});
            skLineSegment(sketch, "E862", {"start": v(-34, -67.98) * mm, "end": v(-10.45, -67.98) * mm});
            skLineSegment(sketch, "E863", {"start": v(-51.12, -60.89) * mm, "end": v(-34, -67.98) * mm});
            skLineSegment(sketch, "E864", {"start": v(-34, -67.98) * mm, "end": v(-16.91, -60.9) * mm});
            skPoint(sketch, "E865", {"position": v(-16.91, -60.9) * mm});
            skLineSegment(sketch, "E866", {"start": v(33.89, -67.98) * mm, "end": v(51.05, -60.87) * mm});
            skPoint(sketch, "E867", {"position": v(51.05, -60.87) * mm});
            skLineSegment(sketch, "E868", {"start": v(33.89, -67.98) * mm, "end": v(47.02, -54.84) * mm});
            skLineSegment(sketch, "E869", {"start": v(33.89, -67.98) * mm, "end": v(41, -50.82) * mm});
            skLineSegment(sketch, "E870", {"start": v(33.89, -49.4) * mm, "end": v(33.89, -67.98) * mm});
            skLineSegment(sketch, "E871", {"start": v(26.78, -50.82) * mm, "end": v(33.89, -67.98) * mm});
            skLineSegment(sketch, "E872", {"start": v(20.75, -54.84) * mm, "end": v(33.89, -67.98) * mm});
            skLineSegment(sketch, "E873", {"start": v(16.72, -60.87) * mm, "end": v(33.89, -67.98) * mm});
            skPoint(sketch, "E874", {"position": v(20.04, -67.98) * mm});
            skPoint(sketch, "E875", {"position": v(24.72, -118.58) * mm});
            skPoint(sketch, "E876", {"position": v(29.35, -118.58) * mm});
            skPoint(sketch, "E877", {"position": v(43.15, -118.58) * mm});
            skLineSegment(sketch, "E878", {"start": v(-5.35, -67.98) * mm, "end": v(-5.35, -118.47) * mm});
            skLineSegment(sketch, "E879", {"start": v(5.16, -69.5) * mm, "end": v(5.16, -118.47) * mm});
            skLineSegment(sketch, "E880", {"start": v(-10.45, -67.98) * mm, "end": v(10.47, -67.98) * mm});
            skLineSegment(sketch, "E881", {"start": v(0.01, -67.98) * mm, "end": v(9.48, -64.05) * mm});
            skLineSegment(sketch, "E882", {"start": v(0.01, -67.98) * mm, "end": v(7.34, -60.65) * mm});
            skLineSegment(sketch, "E883", {"start": v(0.01, -67.98) * mm, "end": v(4.03, -58.29) * mm});
            skLineSegment(sketch, "E884", {"start": v(0.01, -67.98) * mm, "end": v(0.01, -57.48) * mm});
            skLineSegment(sketch, "E885", {"start": v(0.01, -67.98) * mm, "end": v(-4, -58.3) * mm});
            skLineSegment(sketch, "E886", {"start": v(0.01, -67.98) * mm, "end": v(-7.45, -60.5) * mm});
            skLineSegment(sketch, "E887", {"start": v(0.01, -67.98) * mm, "end": v(-9.77, -63.92) * mm});
            skPoint(sketch, "E888", {"position": v(-10.44, -83.84) * mm});
            skPoint(sketch, "E889", {"position": v(-8, -83.84) * mm});
            skPoint(sketch, "E890", {"position": v(-5.35, -83.84) * mm});
            skPoint(sketch, "E891", {"position": v(-2.72, -83.84) * mm});
            skPoint(sketch, "E892", {"position": v(2.53, -83.84) * mm});
            skPoint(sketch, "E893", {"position": v(5.16, -83.84) * mm});
            skPoint(sketch, "E894", {"position": v(7.8, -83.84) * mm});
            skPoint(sketch, "E895", {"position": v(10.48, -83.84) * mm});
            skPoint(sketch, "E896", {"position": v(15.56, -83.84) * mm});
            skPoint(sketch, "E897", {"position": v(20.13, -83.84) * mm});
            skPoint(sketch, "E898", {"position": v(24.75, -83.84) * mm});
            skPoint(sketch, "E899", {"position": v(29.34, -83.84) * mm});
            skPoint(sketch, "E900", {"position": v(31.57, -83.84) * mm});
            skPoint(sketch, "E901", {"position": v(33.85, -83.84) * mm});
            skPoint(sketch, "E902", {"position": v(36.2, -83.84) * mm});
            skPoint(sketch, "E903", {"position": v(38.52, -83.84) * mm});
            skPoint(sketch, "E904", {"position": v(43.15, -83.84) * mm});
            skPoint(sketch, "E905", {"position": v(47.76, -83.84) * mm});
            skLineSegment(sketch, "E906", {"start": v(15.56, -83.84) * mm, "end": v(15.56, -94.04) * mm});
            skLineSegment(sketch, "E907", {"start": v(15.56, -94.04) * mm, "end": v(20.13, -94.04) * mm});
            skLineSegment(sketch, "E908", {"start": v(20.13, -94.04) * mm, "end": v(20.13, -83.84) * mm});
            skLineSegment(sketch, "E909", {"start": v(24.75, -83.84) * mm, "end": v(24.75, -94.04) * mm});
            skLineSegment(sketch, "E910", {"start": v(24.75, -94.04) * mm, "end": v(29.35, -94.04) * mm});
            skLineSegment(sketch, "E911", {"start": v(29.35, -94.04) * mm, "end": v(29.34, -83.84) * mm});
            skLineSegment(sketch, "E912", {"start": v(15.56, -81.78) * mm, "end": v(20.13, -81.78) * mm});
            skLineSegment(sketch, "E913", {"start": v(24.75, -81.78) * mm, "end": v(29.34, -81.78) * mm});
            skLineSegment(sketch, "E914", {"start": v(31.67, -81.78) * mm, "end": v(34.05, -81.78) * mm});
            skLineSegment(sketch, "E915", {"start": v(34.05, -81.78) * mm, "end": v(36.3, -81.78) * mm});
            skLineSegment(sketch, "E916", {"start": v(43.15, -81.84) * mm, "end": v(43.15, -81.84) * mm});
            skPoint(sketch, "E917", {"position": v(28.54, -55.08) * mm});
            skPoint(sketch, "E918", {"position": v(33.89, -54.05) * mm});
            skPoint(sketch, "E919", {"position": v(39.2, -55.14) * mm});
            skPoint(sketch, "E920", {"position": v(43.75, -58.11) * mm});
            skPoint(sketch, "E921", {"position": v(47.02, -54.84) * mm});
            skPoint(sketch, "E922", {"position": v(24.07, -58.16) * mm});
            skPoint(sketch, "E923", {"position": v(27.34, -61.43) * mm});
            skPoint(sketch, "E924", {"position": v(30.33, -59.4) * mm});
            skPoint(sketch, "E925", {"position": v(33.89, -58.7) * mm});
            skPoint(sketch, "E926", {"position": v(37.43, -59.43) * mm});
            skPoint(sketch, "E927", {"position": v(40.43, -61.43) * mm});
            skPoint(sketch, "E928", {"position": v(42.47, -64.43) * mm});
            skPoint(sketch, "E929", {"position": v(46.73, -62.66) * mm});
            skPoint(sketch, "E930", {"position": v(25.33, -64.44) * mm});
            skPoint(sketch, "E931", {"position": v(21.05, -62.66) * mm});
            skPoint(sketch, "E932", {"position": v(16.72, -60.87) * mm});
            skPoint(sketch, "E933", {"position": v(15.3, -67.98) * mm});
            skPoint(sketch, "E934", {"position": v(15.56, -71.59) * mm});
            skPoint(sketch, "E935", {"position": v(20.13, -71.59) * mm});
            skPoint(sketch, "E936", {"position": v(24.74, -71.59) * mm});
            skPoint(sketch, "E937", {"position": v(29.33, -71.59) * mm});
            skPoint(sketch, "E938", {"position": v(31.67, -71.59) * mm});
            skPoint(sketch, "E939", {"position": v(33.95, -71.59) * mm});
            skPoint(sketch, "E940", {"position": v(36.3, -71.59) * mm});
            skPoint(sketch, "E941", {"position": v(43.15, -71.59) * mm});
            skLineSegment(sketch, "E942", {"start": v(31.67, -71.59) * mm, "end": v(36.3, -71.59) * mm});
            skLineSegment(sketch, "E943", {"start": v(24.74, -71.59) * mm, "end": v(24.75, -81.78) * mm});
            skLineSegment(sketch, "E944.bottom", {"start": v(15.53, -96.12) * mm, "end": v(20.13, -96.12) * mm});
            skLineSegment(sketch, "E944.top", {"start": v(15.53, -106.37) * mm, "end": v(20.13, -106.37) * mm});
            skLineSegment(sketch, "E944.left", {"start": v(15.53, -96.12) * mm, "end": v(15.53, -106.37) * mm});
            skLineSegment(sketch, "E944.right", {"start": v(20.13, -96.12) * mm, "end": v(20.13, -106.37) * mm});
            skPoint(sketch, "E945", {"position": v(24.7, -106.28) * mm});
            skPoint(sketch, "E946", {"position": v(29.3, -106.32) * mm});
            skPoint(sketch, "E947", {"position": v(31.67, -106.28) * mm});
            skPoint(sketch, "E948", {"position": v(33.98, -106.32) * mm});
            skPoint(sketch, "E949", {"position": v(36.3, -106.32) * mm});
            skPoint(sketch, "E950", {"position": v(38.61, -106.32) * mm});
            skPoint(sketch, "E951", {"position": v(43.15, -106.32) * mm});
            skPoint(sketch, "E952", {"position": v(0.02, -108.34) * mm});
            skPoint(sketch, "E953", {"position": v(2.54, -108.34) * mm});
            skPoint(sketch, "E954", {"position": v(5.16, -108.34) * mm});
            skPoint(sketch, "E955", {"position": v(7.8, -108.34) * mm});
            skPoint(sketch, "E956", {"position": v(10.47, -108.34) * mm});
            skPoint(sketch, "E957", {"position": v(15.56, -108.34) * mm});
            skPoint(sketch, "E958", {"position": v(20.13, -108.34) * mm});
            skPoint(sketch, "E959", {"position": v(24.7, -108.34) * mm});
            skPoint(sketch, "E960", {"position": v(29.34, -108.34) * mm});
            skPoint(sketch, "E961", {"position": v(31.67, -108.34) * mm});
            skPoint(sketch, "E962", {"position": v(43.15, -108.34) * mm});
            skLineSegment(sketch, "E963", {"start": v(15.56, -71.59) * mm, "end": v(20.13, -71.59) * mm});
            skLineSegment(sketch, "E964", {"start": v(24.74, -71.59) * mm, "end": v(29.33, -71.59) * mm});
            skLineSegment(sketch, "E965", {"start": v(43.15, -71.59) * mm, "end": v(43.15, -71.59) * mm});
            skLineSegment(sketch, "E966", {"start": v(15.56, -71.59) * mm, "end": v(15.56, -81.78) * mm});
            skLineSegment(sketch, "E967", {"start": v(20.13, -71.59) * mm, "end": v(20.13, -81.78) * mm});
            skLineSegment(sketch, "E968", {"start": v(29.33, -71.59) * mm, "end": v(29.34, -81.78) * mm});
            skLineSegment(sketch, "E969", {"start": v(43.15, -71.59) * mm, "end": v(43.15, -81.84) * mm});
            skLineSegment(sketch, "E970", {"start": v(24.75, -83.84) * mm, "end": v(29.34, -83.84) * mm});
            skLineSegment(sketch, "E971", {"start": v(15.56, -83.84) * mm, "end": v(20.13, -83.84) * mm});
            skLineSegment(sketch, "E972", {"start": v(31.57, -94) * mm, "end": v(36.2, -94) * mm});
            skLineSegment(sketch, "E973", {"start": v(38.52, -94) * mm, "end": v(43.15, -94.07) * mm});
            skLineSegment(sketch, "E974", {"start": v(31.67, -71.59) * mm, "end": v(31.67, -81.78) * mm});
            skLineSegment(sketch, "E975", {"start": v(31.57, -83.84) * mm, "end": v(31.57, -94) * mm});
            skLineSegment(sketch, "E976", {"start": v(31.57, -83.84) * mm, "end": v(36.2, -83.84) * mm});
            skLineSegment(sketch, "E977", {"start": v(38.52, -83.84) * mm, "end": v(43.15, -83.84) * mm});
            skLineSegment(sketch, "E978", {"start": v(38.52, -83.84) * mm, "end": v(38.52, -94) * mm});
            skPoint(sketch, "E979", {"position": v(24.71, -96.04) * mm});
            skPoint(sketch, "E980", {"position": v(29.35, -96.1) * mm});
            skPoint(sketch, "E981", {"position": v(36.24, -96.1) * mm});
            skPoint(sketch, "E982", {"position": v(38.58, -96.1) * mm});
            skPoint(sketch, "E983", {"position": v(43.15, -96.1) * mm});
            skLineSegment(sketch, "E984", {"start": v(36.3, -71.59) * mm, "end": v(36.3, -81.78) * mm});
            skLineSegment(sketch, "E985", {"start": v(36.2, -83.84) * mm, "end": v(36.2, -94) * mm});
            skLineSegment(sketch, "E986", {"start": v(24.71, -96.04) * mm, "end": v(24.7, -106.28) * mm});
            skLineSegment(sketch, "E987", {"start": v(29.35, -96.1) * mm, "end": v(29.3, -106.32) * mm});
            skLineSegment(sketch, "E988", {"start": v(24.71, -96.04) * mm, "end": v(29.35, -96.1) * mm});
            skLineSegment(sketch, "E989", {"start": v(24.7, -106.28) * mm, "end": v(29.3, -106.32) * mm});
            skLineSegment(sketch, "E990", {"start": v(38.58, -96.1) * mm, "end": v(38.61, -106.32) * mm});
            skLineSegment(sketch, "E991", {"start": v(38.58, -96.1) * mm, "end": v(43.15, -96.1) * mm});
            skLineSegment(sketch, "E992", {"start": v(43.15, -106.32) * mm, "end": v(38.61, -106.32) * mm});
            skLineSegment(sketch, "E993", {"start": v(36.24, -96.1) * mm, "end": v(36.3, -106.32) * mm});
            skLineSegment(sketch, "E994", {"start": v(31.67, -106.28) * mm, "end": v(31.64, -96.04) * mm});
            skLineSegment(sketch, "E995", {"start": v(31.64, -96.04) * mm, "end": v(36.24, -96.1) * mm});
            skLineSegment(sketch, "E996", {"start": v(31.67, -106.28) * mm, "end": v(36.3, -106.32) * mm});
            skLineSegment(sketch, "E997", {"start": v(15.56, -108.34) * mm, "end": v(15.6, -118.54) * mm});
            skLineSegment(sketch, "E998", {"start": v(15.6, -118.54) * mm, "end": v(20.1, -118.56) * mm});
            skLineSegment(sketch, "E999", {"start": v(20.1, -118.56) * mm, "end": v(20.13, -108.34) * mm});
            skLineSegment(sketch, "E1000", {"start": v(15.56, -108.34) * mm, "end": v(20.13, -108.34) * mm});
            skLineSegment(sketch, "E1001", {"start": v(24.7, -108.34) * mm, "end": v(29.34, -108.34) * mm});
            skLineSegment(sketch, "E1002", {"start": v(29.35, -118.58) * mm, "end": v(24.72, -118.58) * mm});
            skLineSegment(sketch, "E1003", {"start": v(24.7, -108.34) * mm, "end": v(24.72, -118.58) * mm});
            skLineSegment(sketch, "E1004", {"start": v(29.34, -108.34) * mm, "end": v(29.35, -118.58) * mm});
            skPoint(sketch, "E1005", {"position": v(52.3, -83.81) * mm});
            skPoint(sketch, "E1006", {"position": v(47.76, -94.06) * mm});
            skPoint(sketch, "E1007", {"position": v(52.34, -94.06) * mm});
            skPoint(sketch, "E1008", {"position": v(47.76, -96.08) * mm});
            skPoint(sketch, "E1009", {"position": v(52.36, -96.08) * mm});
            skPoint(sketch, "E1010", {"position": v(47.76, -106.34) * mm});
            skPoint(sketch, "E1011", {"position": v(52.36, -106.34) * mm});
            skPoint(sketch, "E1012", {"position": v(47.76, -108.34) * mm});
            skPoint(sketch, "E1013", {"position": v(52.36, -108.34) * mm});
            skPoint(sketch, "E1014", {"position": v(36.2, -108.35) * mm});
            skPoint(sketch, "E1015", {"position": v(38.52, -108.31) * mm});
            skPoint(sketch, "E1016", {"position": v(31.64, -118.58) * mm});
            skPoint(sketch, "E1017", {"position": v(36.2, -118.58) * mm});
            skPoint(sketch, "E1018", {"position": v(47.7, -118.58) * mm});
            skPoint(sketch, "E1019", {"position": v(52.34, -118.58) * mm});
            skLineSegment(sketch, "E1020", {"start": v(31.64, -118.58) * mm, "end": v(36.2, -118.58) * mm});
            skLineSegment(sketch, "E1021", {"start": v(38.46, -118.58) * mm, "end": v(43.15, -118.58) * mm});
            skLineSegment(sketch, "E1022", {"start": v(47.7, -118.58) * mm, "end": v(52.34, -118.58) * mm});
            skLineSegment(sketch, "E1023", {"start": v(31.67, -108.34) * mm, "end": v(36.2, -108.35) * mm});
            skLineSegment(sketch, "E1024", {"start": v(31.67, -108.34) * mm, "end": v(31.64, -118.58) * mm});
            skLineSegment(sketch, "E1025", {"start": v(36.2, -108.35) * mm, "end": v(36.2, -118.58) * mm});
            skLineSegment(sketch, "E1026", {"start": v(38.52, -108.31) * mm, "end": v(38.46, -118.58) * mm});
            skLineSegment(sketch, "E1027", {"start": v(43.15, -118.58) * mm, "end": v(43.15, -108.34) * mm});
            skLineSegment(sketch, "E1028", {"start": v(43.15, -108.34) * mm, "end": v(38.52, -108.31) * mm});
            skLineSegment(sketch, "E1029", {"start": v(47.76, -108.34) * mm, "end": v(52.36, -108.34) * mm});
            skLineSegment(sketch, "E1030", {"start": v(52.34, -118.58) * mm, "end": v(47.7, -118.58) * mm});
            skLineSegment(sketch, "E1031", {"start": v(47.7, -118.58) * mm, "end": v(47.76, -108.34) * mm});
            skLineSegment(sketch, "E1032", {"start": v(52.36, -108.34) * mm, "end": v(52.34, -118.58) * mm});
            skLineSegment(sketch, "E1033", {"start": v(47.76, -96.08) * mm, "end": v(52.36, -96.08) * mm});
            skLineSegment(sketch, "E1034", {"start": v(52.36, -106.34) * mm, "end": v(52.36, -96.08) * mm});
            skLineSegment(sketch, "E1035", {"start": v(47.76, -96.08) * mm, "end": v(47.76, -106.34) * mm});
            skLineSegment(sketch, "E1036", {"start": v(47.76, -106.34) * mm, "end": v(47.76, -96.08) * mm});
            skLineSegment(sketch, "E1037", {"start": v(47.76, -106.34) * mm, "end": v(52.36, -106.34) * mm});
            skLineSegment(sketch, "E1038", {"start": v(47.76, -83.84) * mm, "end": v(47.76, -94.06) * mm});
            skLineSegment(sketch, "E1039", {"start": v(52.34, -94.06) * mm, "end": v(52.3, -83.81) * mm});
            skLineSegment(sketch, "E1040", {"start": v(52.3, -83.81) * mm, "end": v(52.34, -94.06) * mm});
            skLineSegment(sketch, "E1041", {"start": v(52.34, -94.06) * mm, "end": v(47.76, -94.06) * mm});
            skLineSegment(sketch, "E1042", {"start": v(47.76, -83.84) * mm, "end": v(52.3, -83.81) * mm});
            skPoint(sketch, "E1043", {"position": v(47.86, -67.98) * mm});
            skPoint(sketch, "E1044", {"position": v(38.52, -81.81) * mm});
            skPoint(sketch, "E1045", {"position": v(47.85, -71.53) * mm});
            skPoint(sketch, "E1046", {"position": v(52.42, -71.6) * mm});
            skPoint(sketch, "E1047", {"position": v(47.87, -81.81) * mm});
            skPoint(sketch, "E1048", {"position": v(52.47, -81.83) * mm});
            skPoint(sketch, "E1049", {"position": v(38.52, -71.59) * mm});
            skLineSegment(sketch, "E1050", {"start": v(38.52, -71.59) * mm, "end": v(43.15, -71.59) * mm});
            skLineSegment(sketch, "E1051", {"start": v(38.52, -71.59) * mm, "end": v(38.52, -81.81) * mm});
            skLineSegment(sketch, "E1052", {"start": v(38.52, -81.81) * mm, "end": v(43.15, -81.84) * mm});
            skLineSegment(sketch, "E1053", {"start": v(47.85, -71.53) * mm, "end": v(52.42, -71.6) * mm});
            skLineSegment(sketch, "E1054", {"start": v(52.47, -81.83) * mm, "end": v(47.87, -81.81) * mm});
            skLineSegment(sketch, "E1055", {"start": v(47.85, -71.53) * mm, "end": v(47.87, -81.81) * mm});
            skLineSegment(sketch, "E1056", {"start": v(52.42, -71.6) * mm, "end": v(52.47, -81.83) * mm});
            skLineSegment(sketch, "E1057", {"start": v(52.46, -67.98) * mm, "end": v(57.5, -67.99) * mm});
            skLineSegment(sketch, "E1058", {"start": v(15.3, -67.98) * mm, "end": v(10.47, -67.98) * mm});
            skLineSegment(sketch, "E1059", {"start": v(10.47, -67.98) * mm, "end": v(31.57, -67.98) * mm});
            skLineSegment(sketch, "E1060", {"start": v(36.2, -67.98) * mm, "end": v(57.5, -67.99) * mm});
            skPoint(sketch, "E1061", {"position": v(31.55, -69.55) * mm});
            skPoint(sketch, "E1062", {"position": v(36.2, -69.55) * mm});
            skLineSegment(sketch, "E1063", {"start": v(31.57, -67.98) * mm, "end": v(31.55, -69.55) * mm});
            skLineSegment(sketch, "E1064", {"start": v(36.2, -67.98) * mm, "end": v(36.2, -69.55) * mm});
            skLineSegment(sketch, "E1065", {"start": v(36.2, -69.55) * mm, "end": v(31.55, -69.55) * mm});
            skLineSegment(sketch, "E1066", {"start": v(43.15, -67.99) * mm, "end": v(57.5, -67.99) * mm});
            skLineSegment(sketch, "E1067", {"start": v(-8, -67.98) * mm, "end": v(-5.35, -67.98) * mm});
            skLineSegment(sketch, "E1068", {"start": v(5.25, -67.98) * mm, "end": v(7.82, -67.98) * mm});
            skPoint(sketch, "E1069", {"position": v(0.02, -83.84) * mm});
            skPoint(sketch, "E1070", {"position": v(-20.04, -72) * mm});
            skPoint(sketch, "E1071", {"position": v(-15.54, -71.93) * mm});
            skLineSegment(sketch, "E1072", {"start": v(-20.04, -72) * mm, "end": v(-15.54, -71.93) * mm});
            skLineSegment(sketch, "E1073", {"start": v(-15.54, -71.93) * mm, "end": v(-15.53, -81.8) * mm});
            skLineSegment(sketch, "E1074", {"start": v(-20.04, -72) * mm, "end": v(-20.08, -81.8) * mm});
            skPoint(sketch, "E1075", {"position": v(-8, -108.35) * mm});
            skPoint(sketch, "E1076", {"position": v(-5.35, -108.35) * mm});
            skPoint(sketch, "E1077", {"position": v(-2.72, -108.34) * mm});
            skPoint(sketch, "E1078", {"position": v(-10.44, -108.35) * mm});
            skLineSegment(sketch, "E1079", {"start": v(43.15, -83.84) * mm, "end": v(43.15, -94.07) * mm});
            skLineSegment(sketch, "E1080", {"start": v(43.15, -96.1) * mm, "end": v(43.15, -106.32) * mm});
            skPoint(sketch, "E1081", {"position": v(0.02, -106.3) * mm});
            skPoint(sketch, "E1082", {"position": v(-10.45, -81.8) * mm});
            skPoint(sketch, "E1083", {"position": v(-8, -81.8) * mm});
            skPoint(sketch, "E1084", {"position": v(-5.35, -81.8) * mm});
            skPoint(sketch, "E1085", {"position": v(-2.72, -81.8) * mm});
            skPoint(sketch, "E1086", {"position": v(0, -81.8) * mm});
            skPoint(sketch, "E1087", {"position": v(2.53, -81.8) * mm});
            skPoint(sketch, "E1088", {"position": v(5.16, -81.8) * mm});
            skPoint(sketch, "E1089", {"position": v(7.8, -81.8) * mm});
            skPoint(sketch, "E1090", {"position": v(10.47, -81.8) * mm});
            skPoint(sketch, "E1091", {"position": v(-10.44, -94.1) * mm});
            skPoint(sketch, "E1092", {"position": v(-8, -94.09) * mm});
            skPoint(sketch, "E1093", {"position": v(-5.35, -94.08) * mm});
            skPoint(sketch, "E1094", {"position": v(-2.72, -94.1) * mm});
            skPoint(sketch, "E1095", {"position": v(0.02, -94.1) * mm});
            skPoint(sketch, "E1096", {"position": v(2.53, -94.1) * mm});
            skPoint(sketch, "E1097", {"position": v(5.16, -94.1) * mm});
            skPoint(sketch, "E1098", {"position": v(7.8, -94.1) * mm});
            skPoint(sketch, "E1099", {"position": v(10.48, -94.1) * mm});
            skLineSegment(sketch, "E1100", {"start": v(-2.72, -81.8) * mm, "end": v(2.53, -81.8) * mm});
            skLineSegment(sketch, "E1101", {"start": v(-2.72, -67.98) * mm, "end": v(-2.72, -81.8) * mm});
            skLineSegment(sketch, "E1102", {"start": v(-10.45, -81.8) * mm, "end": v(-8, -81.8) * mm});
            skLineSegment(sketch, "E1103", {"start": v(2.57, -67.98) * mm, "end": v(2.53, -81.8) * mm});
            skLineSegment(sketch, "E1104", {"start": v(-10.44, -83.84) * mm, "end": v(-8, -83.84) * mm});
            skLineSegment(sketch, "E1105", {"start": v(-10.44, -94.1) * mm, "end": v(-8, -94.09) * mm});
            skLineSegment(sketch, "E1106", {"start": v(-2.72, -83.84) * mm, "end": v(2.53, -83.84) * mm});
            skLineSegment(sketch, "E1107", {"start": v(2.53, -94.1) * mm, "end": v(-2.72, -94.1) * mm});
            skLineSegment(sketch, "E1108", {"start": v(-2.72, -83.84) * mm, "end": v(-2.72, -94.1) * mm});
            skLineSegment(sketch, "E1109", {"start": v(2.53, -83.84) * mm, "end": v(2.53, -94.1) * mm});
            skPoint(sketch, "E1110", {"position": v(-2.74, -106.32) * mm});
            skPoint(sketch, "E1111", {"position": v(2.52, -106.33) * mm});
            skPoint(sketch, "E1112", {"position": v(-10.44, -96.04) * mm});
            skPoint(sketch, "E1113", {"position": v(-5.35, -96.04) * mm});
            skPoint(sketch, "E1114", {"position": v(-2.76, -96.04) * mm});
            skPoint(sketch, "E1115", {"position": v(2.59, -96.04) * mm});
            skPoint(sketch, "E1116", {"position": v(5.16, -96.04) * mm});
            skPoint(sketch, "E1117", {"position": v(10.48, -96.04) * mm});
            skPoint(sketch, "E1118", {"position": v(10.48, -106.26) * mm});
            skPoint(sketch, "E1119", {"position": v(5.16, -106.26) * mm});
            skPoint(sketch, "E1120", {"position": v(-5.35, -106.26) * mm});
            skPoint(sketch, "E1121", {"position": v(-10.44, -106.26) * mm});
            skPoint(sketch, "E1122", {"position": v(7.8, -96.07) * mm});
            skPoint(sketch, "E1123", {"position": v(7.8, -106.34) * mm});
            skLineSegment(sketch, "E1124", {"start": v(-8, -83.84) * mm, "end": v(-8, -94.09) * mm});
            skLineSegment(sketch, "E1125", {"start": v(-10.44, -94.1) * mm, "end": v(-10.44, -83.84) * mm});
            skLineSegment(sketch, "E1126", {"start": v(-10.44, -96.04) * mm, "end": v(-10.44, -106.26) * mm});
            skLineSegment(sketch, "E1127", {"start": v(-8, -106.26) * mm, "end": v(-8.02, -96.04) * mm});
            skLineSegment(sketch, "E1128", {"start": v(-8.02, -96.04) * mm, "end": v(-10.44, -96.04) * mm});
            skLineSegment(sketch, "E1129", {"start": v(-10.44, -108.35) * mm, "end": v(-10.41, -118.5) * mm});
            skLineSegment(sketch, "E1130", {"start": v(-10.41, -118.5) * mm, "end": v(-8, -118.5) * mm});
            skLineSegment(sketch, "E1131", {"start": v(-8, -118.5) * mm, "end": v(-8, -108.35) * mm});
            skLineSegment(sketch, "E1132", {"start": v(-2.76, -96.04) * mm, "end": v(2.59, -96.04) * mm});
            skLineSegment(sketch, "E1133", {"start": v(2.59, -96.04) * mm, "end": v(2.52, -106.33) * mm});
            skLineSegment(sketch, "E1134", {"start": v(2.55, -106.27) * mm, "end": v(-2.74, -106.32) * mm});
            skLineSegment(sketch, "E1135", {"start": v(-2.74, -106.32) * mm, "end": v(-2.76, -96.04) * mm});
            skLineSegment(sketch, "E1136", {"start": v(-2.72, -108.34) * mm, "end": v(2.54, -108.34) * mm});
            skLineSegment(sketch, "E1137", {"start": v(-2.72, -118.6) * mm, "end": v(-2.72, -108.34) * mm});
            skPoint(sketch, "E1138", {"position": v(2.52, -118.6) * mm});
            skLineSegment(sketch, "E1139", {"start": v(-2.72, -118.6) * mm, "end": v(2.52, -118.6) * mm});
            skLineSegment(sketch, "E1140", {"start": v(2.52, -118.6) * mm, "end": v(2.54, -108.34) * mm});
            skLineSegment(sketch, "E1141", {"start": v(-10.44, -106.26) * mm, "end": v(-8, -106.26) * mm});
            skLineSegment(sketch, "E1142", {"start": v(-10.44, -108.35) * mm, "end": v(-8, -108.35) * mm});
            skLineSegment(sketch, "E1143", {"start": v(7.8, -83.84) * mm, "end": v(10.48, -83.84) * mm});
            skLineSegment(sketch, "E1144", {"start": v(7.8, -94.1) * mm, "end": v(10.48, -94.1) * mm});
            skLineSegment(sketch, "E1145", {"start": v(7.8, -81.8) * mm, "end": v(10.47, -81.8) * mm});
            skLineSegment(sketch, "E1146", {"start": v(7.8, -96.07) * mm, "end": v(10.48, -96.04) * mm});
            skLineSegment(sketch, "E1147", {"start": v(7.8, -106.34) * mm, "end": v(10.48, -106.26) * mm});
            skLineSegment(sketch, "E1148", {"start": v(10.48, -83.84) * mm, "end": v(10.48, -94.1) * mm});
            skLineSegment(sketch, "E1149", {"start": v(10.48, -96.04) * mm, "end": v(10.48, -106.26) * mm});
            skLineSegment(sketch, "E1150", {"start": v(10.47, -108.34) * mm, "end": v(10.47, -118.4) * mm});
            skLineSegment(sketch, "E1151", {"start": v(7.8, -108.34) * mm, "end": v(10.47, -108.34) * mm});
            skLineSegment(sketch, "E1152", {"start": v(10.47, -118.4) * mm, "end": v(7.8, -118.47) * mm});
            skLineSegment(sketch, "E1153", {"start": v(-10.45, -67.98) * mm, "end": v(-10.45, -81.8) * mm});
            skLineSegment(sketch, "E1154", {"start": v(10.47, -67.98) * mm, "end": v(10.47, -81.8) * mm});
            skLineSegment(sketch, "E1155", {"start": v(8.02, -67.98) * mm, "end": v(7.8, -81.8) * mm});
            skLineSegment(sketch, "E1156", {"start": v(7.8, -83.84) * mm, "end": v(7.8, -94.1) * mm});
            skLineSegment(sketch, "E1157", {"start": v(7.8, -96.07) * mm, "end": v(7.8, -106.34) * mm});
            skLineSegment(sketch, "E1158", {"start": v(7.8, -108.34) * mm, "end": v(7.8, -118.47) * mm});
            skPoint(sketch, "E1159", {"position": v(-8.04, -74.66) * mm});
            skLineSegment(sketch, "E1160", {"start": v(-8.04, -74.66) * mm, "end": v(-8, -81.8) * mm});
            skLineSegment(sketch, "E1161", {"start": v(-8, -81.8) * mm, "end": v(-8.04, -74.66) * mm});
            skPoint(sketch, "E1162", {"position": v(3.98, -52.76) * mm});
            skPoint(sketch, "E1163", {"position": v(4.28, -52.07) * mm});
            skPoint(sketch, "E1164", {"position": v(64.56, 6.22) * mm});
            skSolve(sketch);
        }
        {
            var Q0;
            {var subQ0=sQuery(id+"F1.wireOp",EDGE,"E110");Q0=makeQuery(id+"F1.imprint","IMPRINT",FACE,{"disambiguationData":[TD([[makeQuery(id+"F1.imprint","IMPRINT",EDGE,{"derivedFrom":subQ0}),1.0]])]});}
            var Q1;
            {var subQ14=sQuery(id+"F7.wireOp",EDGE,"E652.right");Q1=makeQuery(id+"F7.imprint","IMPRINT",FACE,{"disambiguationData":[TD([[makeQuery(id+"F7.imprint","IMPRINT",EDGE,{"derivedFrom":subQ14}),1.0]])]});}
            var Q2;
            {var subQ11=sQuery(id+"F7.wireOp",EDGE,"pZeGjCGm-WElQ-uWf7-oS4G-AgP7iqahi8NO");Q2=makeQuery(id+"F7.imprint","IMPRINT",FACE,{"disambiguationData":[TD([[makeQuery(id+"F7.imprint","IMPRINT",EDGE,{"derivedFrom":subQ11}),1.0]])]});}
            var Q3;
            {var subQ0=sQuery(id+"F7.wireOp",EDGE,"E873");var subQ1=sQuery(id+"F7.wireOp",EDGE,"E691");var subQ2=makeQuery(id+"F7.imprint","INTERSECT",VERTEX,{"derivedFrom":[subQ1,subQ0]});Q3=makeQuery(id+"F7.imprint","IMPRINT",FACE,{"disambiguationData":[TD([[makeQuery(id+"F7.imprint","IMPRINT",EDGE,{"disambiguationData":[TD([[subQ2,-1.0]])],"derivedFrom":subQ1}),-1.0]])]});}
            var Q4;
            {var subQ0=sQuery(id+"F7.wireOp",EDGE,"E872");var subQ1=sQuery(id+"F7.wireOp",EDGE,"E691");var subQ2=makeQuery(id+"F7.imprint","INTERSECT",VERTEX,{"derivedFrom":[subQ1,subQ0]});Q4=makeQuery(id+"F7.imprint","IMPRINT",FACE,{"disambiguationData":[TD([[makeQuery(id+"F7.imprint","IMPRINT",EDGE,{"disambiguationData":[TD([[subQ2,-1.0]])],"derivedFrom":subQ1}),-1.0]])]});}
            var Q5;
            {var subQ0=sQuery(id+"F7.wireOp",EDGE,"E870");var subQ1=sQuery(id+"F7.wireOp",EDGE,"E691");var subQ2=makeQuery(id+"F7.imprint","INTERSECT",VERTEX,{"derivedFrom":[subQ1,subQ0]});Q5=makeQuery(id+"F7.imprint","IMPRINT",FACE,{"disambiguationData":[TD([[makeQuery(id+"F7.imprint","IMPRINT",EDGE,{"disambiguationData":[TD([[subQ2,-1.0]])],"derivedFrom":subQ1}),-1.0]])]});}
            var Q6;
            {var subQ0=sQuery(id+"F7.wireOp",EDGE,"E871");var subQ1=sQuery(id+"F7.wireOp",EDGE,"E691");var subQ2=makeQuery(id+"F7.imprint","INTERSECT",VERTEX,{"derivedFrom":[subQ1,subQ0]});Q6=makeQuery(id+"F7.imprint","IMPRINT",FACE,{"disambiguationData":[TD([[makeQuery(id+"F7.imprint","IMPRINT",EDGE,{"disambiguationData":[TD([[subQ2,-1.0]])],"derivedFrom":subQ1}),-1.0]])]});}
            var Q7;
            {var subQ0=sQuery(id+"F7.wireOp",EDGE,"E1059");var subQ1=sQuery(id+"F7.wireOp",EDGE,"E691");var subQ2=makeQuery(id+"F7.imprint","INTERSECT",VERTEX,{"derivedFrom":[subQ1,subQ0]});Q7=makeQuery(id+"F7.imprint","IMPRINT",FACE,{"disambiguationData":[TD([[makeQuery(id+"F7.imprint","IMPRINT",EDGE,{"disambiguationData":[TD([[subQ2,-1.0]])],"derivedFrom":subQ1}),-1.0]])]});}
            var Q8;
            {var subQ0=sQuery(id+"F7.wireOp",EDGE,"E869");var subQ1=sQuery(id+"F7.wireOp",EDGE,"E691");var subQ2=makeQuery(id+"F7.imprint","INTERSECT",VERTEX,{"derivedFrom":[subQ1,subQ0]});Q8=makeQuery(id+"F7.imprint","IMPRINT",FACE,{"disambiguationData":[TD([[makeQuery(id+"F7.imprint","IMPRINT",EDGE,{"disambiguationData":[TD([[subQ2,-1.0]])],"derivedFrom":subQ1}),-1.0]])]});}
            var Q9;
            {var subQ0=sQuery(id+"F7.wireOp",EDGE,"E868");var subQ1=sQuery(id+"F7.wireOp",EDGE,"E691");var subQ2=makeQuery(id+"F7.imprint","INTERSECT",VERTEX,{"derivedFrom":[subQ1,subQ0]});Q9=makeQuery(id+"F7.imprint","IMPRINT",FACE,{"disambiguationData":[TD([[makeQuery(id+"F7.imprint","IMPRINT",EDGE,{"disambiguationData":[TD([[subQ2,-1.0]])],"derivedFrom":subQ1}),-1.0]])]});}
            var Q10;
            {var subQ0=sQuery(id+"F7.wireOp",EDGE,"E1060");var subQ1=sQuery(id+"F7.wireOp",EDGE,"E691");var subQ2=makeQuery(id+"F7.imprint","INTERSECT",VERTEX,{"derivedFrom":[subQ1,subQ0]});Q10=makeQuery(id+"F7.imprint","IMPRINT",FACE,{"disambiguationData":[TD([[makeQuery(id+"F7.imprint","IMPRINT",EDGE,{"disambiguationData":[TD([[subQ2,1.0]])],"derivedFrom":subQ1}),-1.0]])]});}
            var Q11;
            {var subQ4=sQuery(id+"F7.wireOp",EDGE,"E652.left");Q11=makeQuery(id+"F7.imprint","IMPRINT",FACE,{"disambiguationData":[TD([[makeQuery(id+"F7.imprint","IMPRINT",EDGE,{"derivedFrom":subQ4}),-1.0]])]});}
            extrude(context, id + "F8", {"entities" : qUnion([Q0, Q1, Q2, Q3, Q4, Q5, Q6, Q7, Q8, Q9, Q10, Q11]), "operationType" : NewBodyOperationType.ADD, "depth" : 4 * mm, "offsetDistance" : 25 * mm});
        }
    });
